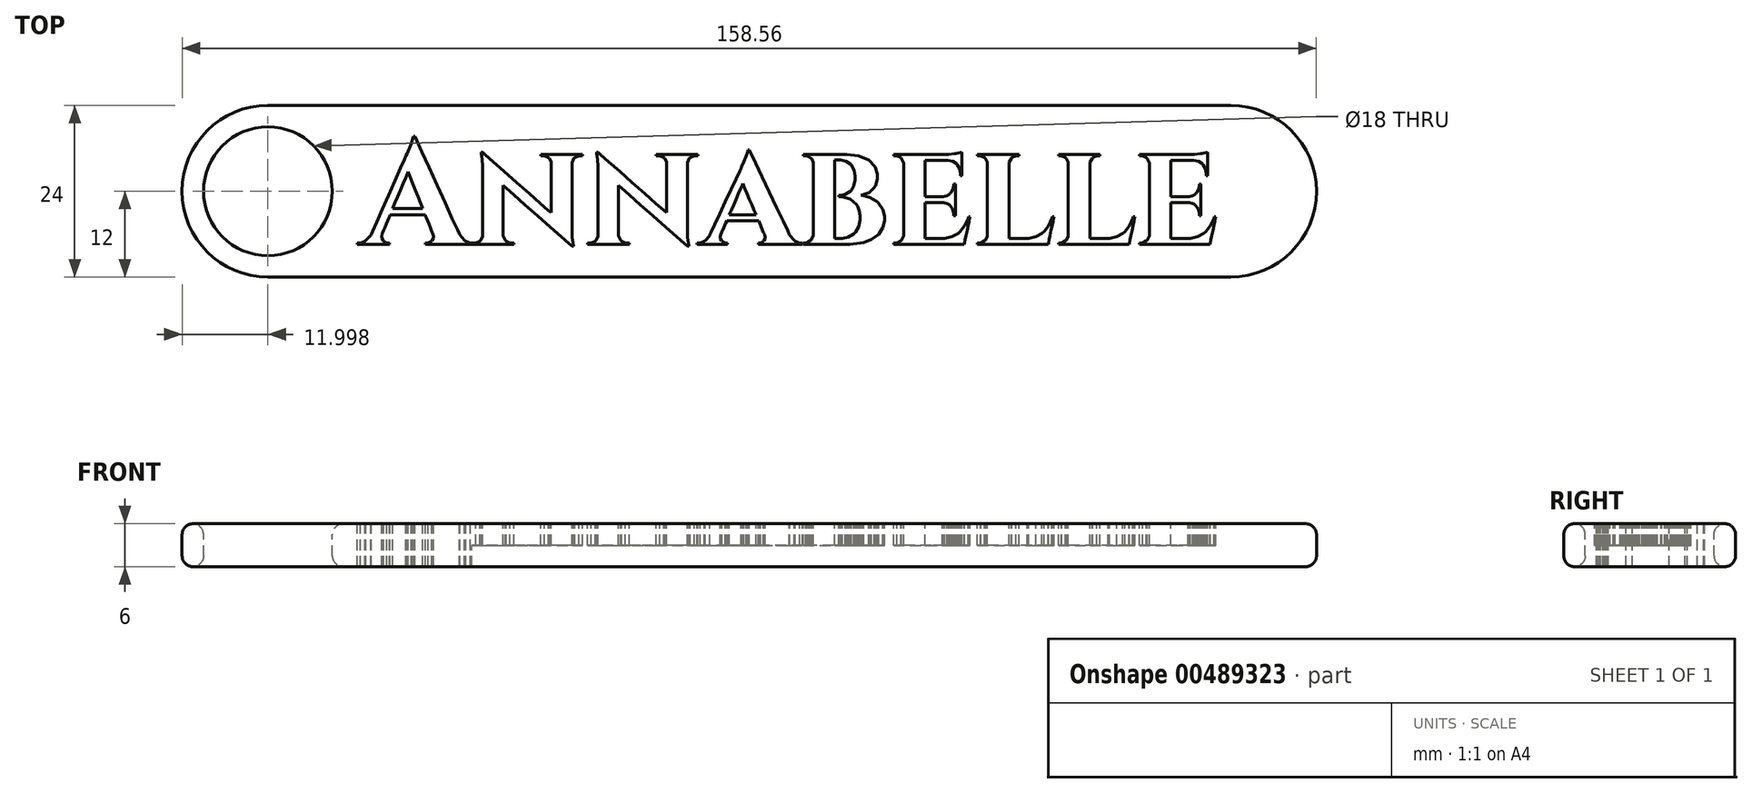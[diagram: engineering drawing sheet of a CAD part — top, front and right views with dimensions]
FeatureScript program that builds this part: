
annotation { "Feature Type Name" : "Feature", "Feature Type Description" : "" }
export const myFeature = defineFeature(function(context is Context, id is Id, definition is map)
    precondition{}
    {
        {
            var Q0;
            Q0=qCreatedBy(makeId("Top.planeOp"),FACE);
            var sketch = newSketch(context, id + "F0", { "sketchPlane" : qUnion([Q0])});
            skLineSegment(sketch, "E0", {"start": v(-43.95, -7.2) * mm, "end": v(-43.76, -7.2) * mm});
            skLineSegment(sketch, "E1", {"start": v(-43.76, -7.2) * mm, "end": v(-43.76, -7.31) * mm});
            skLineSegment(sketch, "E2", {"start": v(-43.76, -7.31) * mm, "end": v(-43.76, -7.42) * mm});
            skLineSegment(sketch, "E3", {"start": v(-43.76, -7.42) * mm, "end": v(-44.05, -7.42) * mm});
            skLineSegment(sketch, "E4", {"start": v(-44.05, -7.42) * mm, "end": v(-44.8, -7.42) * mm});
            skLineSegment(sketch, "E5", {"start": v(-44.8, -7.42) * mm, "end": v(-45.88, -7.42) * mm});
            skLineSegment(sketch, "E6", {"start": v(-45.88, -7.42) * mm, "end": v(-47.1, -7.42) * mm});
            skLineSegment(sketch, "E7", {"start": v(-47.1, -7.42) * mm, "end": v(-48.34, -7.42) * mm});
            skLineSegment(sketch, "E8", {"start": v(-48.34, -7.42) * mm, "end": v(-49.4, -7.42) * mm});
            skLineSegment(sketch, "E9", {"start": v(-49.4, -7.42) * mm, "end": v(-50.17, -7.42) * mm});
            skLineSegment(sketch, "E10", {"start": v(-50.17, -7.42) * mm, "end": v(-50.45, -7.42) * mm});
            skLineSegment(sketch, "E11", {"start": v(-50.45, -7.42) * mm, "end": v(-50.45, -7.31) * mm});
            skLineSegment(sketch, "E12", {"start": v(-50.45, -7.31) * mm, "end": v(-50.45, -7.2) * mm});
            skLineSegment(sketch, "E13", {"start": v(-50.45, -7.2) * mm, "end": v(-50.26, -7.2) * mm});
            skLineSegment(sketch, "E14", {"start": v(-50.26, -7.2) * mm, "end": v(-50.1, -7.2) * mm});
            skLineSegment(sketch, "E15", {"start": v(-50.1, -7.2) * mm, "end": v(-49.62, -6.97) * mm});
            skLineSegment(sketch, "E16", {"start": v(-49.62, -6.97) * mm, "end": v(-49.58, -6.92) * mm});
            skLineSegment(sketch, "E17", {"start": v(-49.58, -6.92) * mm, "end": v(-49.55, -6.88) * mm});
            skLineSegment(sketch, "E18", {"start": v(-49.55, -6.88) * mm, "end": v(-49.36, -6.51) * mm});
            skLineSegment(sketch, "E19", {"start": v(-49.36, -6.51) * mm, "end": v(-49.36, -6.39) * mm});
            skLineSegment(sketch, "E20", {"start": v(-49.36, -6.39) * mm, "end": v(-49.36, -6.26) * mm});
            skLineSegment(sketch, "E21", {"start": v(-49.36, -6.26) * mm, "end": v(-49.45, -5.93) * mm});
            skLineSegment(sketch, "E22", {"start": v(-49.45, -5.93) * mm, "end": v(-49.47, -5.89) * mm});
            skLineSegment(sketch, "E23", {"start": v(-49.47, -5.89) * mm, "end": v(-49.51, -5.77) * mm});
            skLineSegment(sketch, "E24", {"start": v(-49.51, -5.77) * mm, "end": v(-49.63, -5.48) * mm});
            skLineSegment(sketch, "E25", {"start": v(-49.63, -5.48) * mm, "end": v(-49.8, -5.07) * mm});
            skLineSegment(sketch, "E26", {"start": v(-49.8, -5.07) * mm, "end": v(-49.98, -4.6) * mm});
            skLineSegment(sketch, "E27", {"start": v(-49.98, -4.6) * mm, "end": v(-50.17, -4.12) * mm});
            skLineSegment(sketch, "E28", {"start": v(-50.17, -4.12) * mm, "end": v(-50.33, -3.7) * mm});
            skLineSegment(sketch, "E29", {"start": v(-50.33, -3.7) * mm, "end": v(-50.45, -3.42) * mm});
            skLineSegment(sketch, "E30", {"start": v(-50.45, -3.42) * mm, "end": v(-50.5, -3.3) * mm});
            skLineSegment(sketch, "E31", {"start": v(-50.5, -3.3) * mm, "end": v(-50.7, -3.3) * mm});
            skLineSegment(sketch, "E32", {"start": v(-50.7, -3.3) * mm, "end": v(-51.26, -3.3) * mm});
            skLineSegment(sketch, "E33", {"start": v(-51.26, -3.3) * mm, "end": v(-52.05, -3.3) * mm});
            skLineSegment(sketch, "E34", {"start": v(-52.05, -3.3) * mm, "end": v(-52.95, -3.3) * mm});
            skLineSegment(sketch, "E35", {"start": v(-52.95, -3.3) * mm, "end": v(-53.85, -3.3) * mm});
            skLineSegment(sketch, "E36", {"start": v(-53.85, -3.3) * mm, "end": v(-54.64, -3.3) * mm});
            skLineSegment(sketch, "E37", {"start": v(-54.64, -3.3) * mm, "end": v(-55.2, -3.3) * mm});
            skLineSegment(sketch, "E38", {"start": v(-55.2, -3.3) * mm, "end": v(-55.4, -3.3) * mm});
            skLineSegment(sketch, "E39", {"start": v(-55.4, -3.3) * mm, "end": v(-55.45, -3.42) * mm});
            skLineSegment(sketch, "E40", {"start": v(-55.45, -3.42) * mm, "end": v(-55.58, -3.7) * mm});
            skLineSegment(sketch, "E41", {"start": v(-55.58, -3.7) * mm, "end": v(-55.75, -4.12) * mm});
            skLineSegment(sketch, "E42", {"start": v(-55.75, -4.12) * mm, "end": v(-55.95, -4.6) * mm});
            skLineSegment(sketch, "E43", {"start": v(-55.95, -4.6) * mm, "end": v(-56.15, -5.07) * mm});
            skLineSegment(sketch, "E44", {"start": v(-56.15, -5.07) * mm, "end": v(-56.33, -5.48) * mm});
            skLineSegment(sketch, "E45", {"start": v(-56.33, -5.48) * mm, "end": v(-56.45, -5.77) * mm});
            skLineSegment(sketch, "E46", {"start": v(-56.45, -5.77) * mm, "end": v(-56.5, -5.89) * mm});
            skLineSegment(sketch, "E47", {"start": v(-56.5, -5.89) * mm, "end": v(-56.51, -5.93) * mm});
            skLineSegment(sketch, "E48", {"start": v(-56.51, -5.93) * mm, "end": v(-56.6, -6.28) * mm});
            skLineSegment(sketch, "E49", {"start": v(-56.6, -6.28) * mm, "end": v(-56.6, -6.4) * mm});
            skLineSegment(sketch, "E50", {"start": v(-56.6, -6.4) * mm, "end": v(-56.6, -6.53) * mm});
            skLineSegment(sketch, "E51", {"start": v(-56.6, -6.53) * mm, "end": v(-56.4, -6.88) * mm});
            skLineSegment(sketch, "E52", {"start": v(-56.4, -6.88) * mm, "end": v(-56.37, -6.92) * mm});
            skLineSegment(sketch, "E53", {"start": v(-56.37, -6.92) * mm, "end": v(-56.33, -6.97) * mm});
            skLineSegment(sketch, "E54", {"start": v(-56.33, -6.97) * mm, "end": v(-55.84, -7.2) * mm});
            skLineSegment(sketch, "E55", {"start": v(-55.84, -7.2) * mm, "end": v(-55.68, -7.2) * mm});
            skLineSegment(sketch, "E56", {"start": v(-55.68, -7.2) * mm, "end": v(-55.51, -7.2) * mm});
            skLineSegment(sketch, "E57", {"start": v(-55.51, -7.2) * mm, "end": v(-55.51, -7.31) * mm});
            skLineSegment(sketch, "E58", {"start": v(-55.51, -7.31) * mm, "end": v(-55.51, -7.42) * mm});
            skLineSegment(sketch, "E59", {"start": v(-55.51, -7.42) * mm, "end": v(-55.7, -7.42) * mm});
            skLineSegment(sketch, "E60", {"start": v(-55.7, -7.42) * mm, "end": v(-56.21, -7.42) * mm});
            skLineSegment(sketch, "E61", {"start": v(-56.21, -7.42) * mm, "end": v(-56.93, -7.42) * mm});
            skLineSegment(sketch, "E62", {"start": v(-56.93, -7.42) * mm, "end": v(-57.76, -7.42) * mm});
            skLineSegment(sketch, "E63", {"start": v(-57.76, -7.42) * mm, "end": v(-58.58, -7.42) * mm});
            skLineSegment(sketch, "E64", {"start": v(-58.58, -7.42) * mm, "end": v(-59.3, -7.42) * mm});
            skLineSegment(sketch, "E65", {"start": v(-59.3, -7.42) * mm, "end": v(-59.8, -7.42) * mm});
            skLineSegment(sketch, "E66", {"start": v(-59.8, -7.42) * mm, "end": v(-60, -7.42) * mm});
            skLineSegment(sketch, "E67", {"start": v(-60, -7.42) * mm, "end": v(-60, -7.31) * mm});
            skLineSegment(sketch, "E68", {"start": v(-60, -7.31) * mm, "end": v(-60, -7.2) * mm});
            skLineSegment(sketch, "E69", {"start": v(-60, -7.2) * mm, "end": v(-59.81, -7.2) * mm});
            skLineSegment(sketch, "E70", {"start": v(-59.81, -7.2) * mm, "end": v(-59.57, -7.2) * mm});
            skLineSegment(sketch, "E71", {"start": v(-59.57, -7.2) * mm, "end": v(-58.93, -6.96) * mm});
            skLineSegment(sketch, "E72", {"start": v(-58.93, -6.96) * mm, "end": v(-58.85, -6.91) * mm});
            skLineSegment(sketch, "E73", {"start": v(-58.85, -6.91) * mm, "end": v(-58.77, -6.86) * mm});
            skLineSegment(sketch, "E74", {"start": v(-58.77, -6.86) * mm, "end": v(-58.1, -6.13) * mm});
            skLineSegment(sketch, "E75", {"start": v(-58.1, -6.13) * mm, "end": v(-58.05, -6.03) * mm});
            skLineSegment(sketch, "E76", {"start": v(-58.05, -6.03) * mm, "end": v(-57.84, -5.56) * mm});
            skLineSegment(sketch, "E77", {"start": v(-57.84, -5.56) * mm, "end": v(-57.3, -4.32) * mm});
            skLineSegment(sketch, "E78", {"start": v(-57.3, -4.32) * mm, "end": v(-56.52, -2.56) * mm});
            skLineSegment(sketch, "E79", {"start": v(-56.52, -2.56) * mm, "end": v(-55.63, -0.55) * mm});
            skLineSegment(sketch, "E80", {"start": v(-55.63, -0.55) * mm, "end": v(-54.74, 1.47) * mm});
            skLineSegment(sketch, "E81", {"start": v(-54.74, 1.47) * mm, "end": v(-53.96, 3.23) * mm});
            skLineSegment(sketch, "E82", {"start": v(-53.96, 3.23) * mm, "end": v(-53.41, 4.47) * mm});
            skLineSegment(sketch, "E83", {"start": v(-53.41, 4.47) * mm, "end": v(-53.2, 4.94) * mm});
            skLineSegment(sketch, "E84", {"start": v(-53.2, 4.94) * mm, "end": v(-53.04, 5.29) * mm});
            skLineSegment(sketch, "E85", {"start": v(-53.04, 5.29) * mm, "end": v(-52.45, 6.67) * mm});
            skLineSegment(sketch, "E86", {"start": v(-52.45, 6.67) * mm, "end": v(-52.16, 7.58) * mm});
            skLineSegment(sketch, "E87", {"start": v(-52.16, 7.58) * mm, "end": v(-52.15, 7.7) * mm});
            skLineSegment(sketch, "E88", {"start": v(-52.15, 7.7) * mm, "end": v(-51.96, 7.7) * mm});
            skLineSegment(sketch, "E89", {"start": v(-51.96, 7.7) * mm, "end": v(-51.7, 7.1) * mm});
            skLineSegment(sketch, "E90", {"start": v(-51.7, 7.1) * mm, "end": v(-51, 5.55) * mm});
            skLineSegment(sketch, "E91", {"start": v(-51, 5.55) * mm, "end": v(-50, 3.36) * mm});
            skLineSegment(sketch, "E92", {"start": v(-50, 3.36) * mm, "end": v(-48.85, 0.85) * mm});
            skLineSegment(sketch, "E93", {"start": v(-48.85, 0.85) * mm, "end": v(-47.7, -1.66) * mm});
            skLineSegment(sketch, "E94", {"start": v(-47.7, -1.66) * mm, "end": v(-46.7, -3.85) * mm});
            skLineSegment(sketch, "E95", {"start": v(-46.7, -3.85) * mm, "end": v(-46, -5.4) * mm});
            skLineSegment(sketch, "E96", {"start": v(-46, -5.4) * mm, "end": v(-45.73, -6) * mm});
            skLineSegment(sketch, "E97", {"start": v(-45.73, -6) * mm, "end": v(-45.68, -6.1) * mm});
            skLineSegment(sketch, "E98", {"start": v(-45.68, -6.1) * mm, "end": v(-45.02, -6.85) * mm});
            skLineSegment(sketch, "E99", {"start": v(-45.02, -6.85) * mm, "end": v(-44.94, -6.9) * mm});
            skLineSegment(sketch, "E100", {"start": v(-44.94, -6.9) * mm, "end": v(-44.86, -6.95) * mm});
            skLineSegment(sketch, "E101", {"start": v(-44.86, -6.95) * mm, "end": v(-44.18, -7.2) * mm});
            skLineSegment(sketch, "E102", {"start": v(-44.18, -7.2) * mm, "end": v(-43.95, -7.2) * mm});
            skLineSegment(sketch, "E103", {"start": v(-55.05, -2.42) * mm, "end": v(-54.87, -2.42) * mm});
            skLineSegment(sketch, "E104", {"start": v(-54.87, -2.42) * mm, "end": v(-54.4, -2.42) * mm});
            skLineSegment(sketch, "E105", {"start": v(-54.4, -2.42) * mm, "end": v(-53.72, -2.42) * mm});
            skLineSegment(sketch, "E106", {"start": v(-53.72, -2.42) * mm, "end": v(-52.95, -2.42) * mm});
            skLineSegment(sketch, "E107", {"start": v(-52.95, -2.42) * mm, "end": v(-52.18, -2.42) * mm});
            skLineSegment(sketch, "E108", {"start": v(-52.18, -2.42) * mm, "end": v(-51.5, -2.42) * mm});
            skLineSegment(sketch, "E109", {"start": v(-51.5, -2.42) * mm, "end": v(-51.03, -2.42) * mm});
            skLineSegment(sketch, "E110", {"start": v(-51.03, -2.42) * mm, "end": v(-50.85, -2.42) * mm});
            skLineSegment(sketch, "E111", {"start": v(-50.85, -2.42) * mm, "end": v(-50.94, -2.2) * mm});
            skLineSegment(sketch, "E112", {"start": v(-50.94, -2.2) * mm, "end": v(-51.17, -1.62) * mm});
            skLineSegment(sketch, "E113", {"start": v(-51.17, -1.62) * mm, "end": v(-51.5, -0.79) * mm});
            skLineSegment(sketch, "E114", {"start": v(-51.5, -0.79) * mm, "end": v(-51.87, 0.16) * mm});
            skLineSegment(sketch, "E115", {"start": v(-51.87, 0.16) * mm, "end": v(-52.24, 1.1) * mm});
            skLineSegment(sketch, "E116", {"start": v(-52.24, 1.1) * mm, "end": v(-52.57, 1.93) * mm});
            skLineSegment(sketch, "E117", {"start": v(-52.57, 1.93) * mm, "end": v(-52.8, 2.52) * mm});
            skLineSegment(sketch, "E118", {"start": v(-52.8, 2.52) * mm, "end": v(-52.89, 2.74) * mm});
            skLineSegment(sketch, "E119", {"start": v(-52.89, 2.74) * mm, "end": v(-52.98, 2.52) * mm});
            skLineSegment(sketch, "E120", {"start": v(-52.98, 2.52) * mm, "end": v(-53.23, 1.93) * mm});
            skLineSegment(sketch, "E121", {"start": v(-53.23, 1.93) * mm, "end": v(-53.57, 1.1) * mm});
            skLineSegment(sketch, "E122", {"start": v(-53.57, 1.1) * mm, "end": v(-53.97, 0.16) * mm});
            skLineSegment(sketch, "E123", {"start": v(-53.97, 0.16) * mm, "end": v(-54.37, -0.79) * mm});
            skLineSegment(sketch, "E124", {"start": v(-54.37, -0.79) * mm, "end": v(-54.71, -1.62) * mm});
            skLineSegment(sketch, "E125", {"start": v(-54.71, -1.62) * mm, "end": v(-54.96, -2.2) * mm});
            skLineSegment(sketch, "E126", {"start": v(-54.96, -2.2) * mm, "end": v(-55.05, -2.42) * mm});
            skLineSegment(sketch, "E127", {"start": v(-34.38, 5.17) * mm, "end": v(-33.46, 5.17) * mm});
            skLineSegment(sketch, "E128", {"start": v(-33.46, 5.17) * mm, "end": v(-31.43, 5.17) * mm});
            skLineSegment(sketch, "E129", {"start": v(-31.43, 5.17) * mm, "end": v(-29.4, 5.17) * mm});
            skLineSegment(sketch, "E130", {"start": v(-29.4, 5.17) * mm, "end": v(-28.48, 5.17) * mm});
            skLineSegment(sketch, "E131", {"start": v(-28.48, 5.17) * mm, "end": v(-28.48, 5.07) * mm});
            skLineSegment(sketch, "E132", {"start": v(-28.48, 5.07) * mm, "end": v(-28.48, 4.96) * mm});
            skLineSegment(sketch, "E133", {"start": v(-28.48, 4.96) * mm, "end": v(-28.66, 4.96) * mm});
            skLineSegment(sketch, "E134", {"start": v(-28.66, 4.96) * mm, "end": v(-28.84, 4.96) * mm});
            skLineSegment(sketch, "E135", {"start": v(-28.84, 4.96) * mm, "end": v(-29.04, 4.96) * mm});
            skLineSegment(sketch, "E136", {"start": v(-29.04, 4.96) * mm, "end": v(-29.6, 4.72) * mm});
            skLineSegment(sketch, "E137", {"start": v(-29.6, 4.72) * mm, "end": v(-29.65, 4.67) * mm});
            skLineSegment(sketch, "E138", {"start": v(-29.65, 4.67) * mm, "end": v(-29.7, 4.62) * mm});
            skLineSegment(sketch, "E139", {"start": v(-29.7, 4.62) * mm, "end": v(-30, 4) * mm});
            skLineSegment(sketch, "E140", {"start": v(-30, 4) * mm, "end": v(-30, 3.91) * mm});
            skLineSegment(sketch, "E141", {"start": v(-30, 3.91) * mm, "end": v(-30, 3.52) * mm});
            skLineSegment(sketch, "E142", {"start": v(-30, 3.52) * mm, "end": v(-30, 2.48) * mm});
            skLineSegment(sketch, "E143", {"start": v(-30, 2.48) * mm, "end": v(-30, 1.01) * mm});
            skLineSegment(sketch, "E144", {"start": v(-30, 1.01) * mm, "end": v(-30, -0.67) * mm});
            skLineSegment(sketch, "E145", {"start": v(-30, -0.67) * mm, "end": v(-30, -2.35) * mm});
            skLineSegment(sketch, "E146", {"start": v(-30, -2.35) * mm, "end": v(-30, -3.82) * mm});
            skLineSegment(sketch, "E147", {"start": v(-30, -3.82) * mm, "end": v(-30, -4.86) * mm});
            skLineSegment(sketch, "E148", {"start": v(-30, -4.86) * mm, "end": v(-30, -5.26) * mm});
            skLineSegment(sketch, "E149", {"start": v(-30, -5.26) * mm, "end": v(-30, -5.55) * mm});
            skLineSegment(sketch, "E150", {"start": v(-30, -5.55) * mm, "end": v(-29.95, -6.44) * mm});
            skLineSegment(sketch, "E151", {"start": v(-29.95, -6.44) * mm, "end": v(-29.86, -7.26) * mm});
            skLineSegment(sketch, "E152", {"start": v(-29.86, -7.26) * mm, "end": v(-29.83, -7.4) * mm});
            skLineSegment(sketch, "E153", {"start": v(-29.83, -7.4) * mm, "end": v(-29.8, -7.54) * mm});
            skLineSegment(sketch, "E154", {"start": v(-29.8, -7.54) * mm, "end": v(-29.78, -7.7) * mm});
            skLineSegment(sketch, "E155", {"start": v(-29.78, -7.7) * mm, "end": v(-29.97, -7.7) * mm});
            skLineSegment(sketch, "E156", {"start": v(-29.97, -7.7) * mm, "end": v(-30.39, -7.32) * mm});
            skLineSegment(sketch, "E157", {"start": v(-30.39, -7.32) * mm, "end": v(-31.48, -6.36) * mm});
            skLineSegment(sketch, "E158", {"start": v(-31.48, -6.36) * mm, "end": v(-33.02, -5) * mm});
            skLineSegment(sketch, "E159", {"start": v(-33.02, -5) * mm, "end": v(-34.8, -3.44) * mm});
            skLineSegment(sketch, "E160", {"start": v(-34.8, -3.44) * mm, "end": v(-36.56, -1.88) * mm});
            skLineSegment(sketch, "E161", {"start": v(-36.56, -1.88) * mm, "end": v(-38.1, -0.52) * mm});
            skLineSegment(sketch, "E162", {"start": v(-38.1, -0.52) * mm, "end": v(-39.2, 0.44) * mm});
            skLineSegment(sketch, "E163", {"start": v(-39.2, 0.44) * mm, "end": v(-39.6, 0.8) * mm});
            skLineSegment(sketch, "E164", {"start": v(-39.6, 0.8) * mm, "end": v(-39.6, 0.51) * mm});
            skLineSegment(sketch, "E165", {"start": v(-39.6, 0.51) * mm, "end": v(-39.6, -0.28) * mm});
            skLineSegment(sketch, "E166", {"start": v(-39.6, -0.28) * mm, "end": v(-39.6, -1.39) * mm});
            skLineSegment(sketch, "E167", {"start": v(-39.6, -1.39) * mm, "end": v(-39.6, -2.66) * mm});
            skLineSegment(sketch, "E168", {"start": v(-39.6, -2.66) * mm, "end": v(-39.6, -3.94) * mm});
            skLineSegment(sketch, "E169", {"start": v(-39.6, -3.94) * mm, "end": v(-39.6, -5.05) * mm});
            skLineSegment(sketch, "E170", {"start": v(-39.6, -5.05) * mm, "end": v(-39.6, -5.84) * mm});
            skLineSegment(sketch, "E171", {"start": v(-39.6, -5.84) * mm, "end": v(-39.6, -6.14) * mm});
            skLineSegment(sketch, "E172", {"start": v(-39.6, -6.14) * mm, "end": v(-39.6, -6.21) * mm});
            skLineSegment(sketch, "E173", {"start": v(-39.6, -6.21) * mm, "end": v(-39.31, -6.85) * mm});
            skLineSegment(sketch, "E174", {"start": v(-39.31, -6.85) * mm, "end": v(-39.26, -6.9) * mm});
            skLineSegment(sketch, "E175", {"start": v(-39.26, -6.9) * mm, "end": v(-39.2, -6.95) * mm});
            skLineSegment(sketch, "E176", {"start": v(-39.2, -6.95) * mm, "end": v(-38.64, -7.2) * mm});
            skLineSegment(sketch, "E177", {"start": v(-38.64, -7.2) * mm, "end": v(-38.45, -7.2) * mm});
            skLineSegment(sketch, "E178", {"start": v(-38.45, -7.2) * mm, "end": v(-38.27, -7.2) * mm});
            skLineSegment(sketch, "E179", {"start": v(-38.27, -7.2) * mm, "end": v(-38.1, -7.2) * mm});
            skLineSegment(sketch, "E180", {"start": v(-38.1, -7.2) * mm, "end": v(-38.1, -7.31) * mm});
            skLineSegment(sketch, "E181", {"start": v(-38.1, -7.31) * mm, "end": v(-38.1, -7.42) * mm});
            skLineSegment(sketch, "E182", {"start": v(-38.1, -7.42) * mm, "end": v(-39.01, -7.42) * mm});
            skLineSegment(sketch, "E183", {"start": v(-39.01, -7.42) * mm, "end": v(-41.03, -7.42) * mm});
            skLineSegment(sketch, "E184", {"start": v(-41.03, -7.42) * mm, "end": v(-43.05, -7.42) * mm});
            skLineSegment(sketch, "E185", {"start": v(-43.05, -7.42) * mm, "end": v(-43.97, -7.42) * mm});
            skLineSegment(sketch, "E186", {"start": v(-43.97, -7.42) * mm, "end": v(-43.97, -7.31) * mm});
            skLineSegment(sketch, "E187", {"start": v(-43.97, -7.31) * mm, "end": v(-43.97, -7.2) * mm});
            skLineSegment(sketch, "E188", {"start": v(-43.97, -7.2) * mm, "end": v(-43.8, -7.2) * mm});
            skLineSegment(sketch, "E189", {"start": v(-43.8, -7.2) * mm, "end": v(-43.63, -7.2) * mm});
            skLineSegment(sketch, "E190", {"start": v(-43.63, -7.2) * mm, "end": v(-43.43, -7.2) * mm});
            skLineSegment(sketch, "E191", {"start": v(-43.43, -7.2) * mm, "end": v(-42.87, -6.95) * mm});
            skLineSegment(sketch, "E192", {"start": v(-42.87, -6.95) * mm, "end": v(-42.82, -6.9) * mm});
            skLineSegment(sketch, "E193", {"start": v(-42.82, -6.9) * mm, "end": v(-42.76, -6.85) * mm});
            skLineSegment(sketch, "E194", {"start": v(-42.76, -6.85) * mm, "end": v(-42.48, -6.32) * mm});
            skLineSegment(sketch, "E195", {"start": v(-42.48, -6.32) * mm, "end": v(-42.48, -6.14) * mm});
            skLineSegment(sketch, "E196", {"start": v(-42.48, -6.14) * mm, "end": v(-42.48, -5.74) * mm});
            skLineSegment(sketch, "E197", {"start": v(-42.48, -5.74) * mm, "end": v(-42.48, -4.7) * mm});
            skLineSegment(sketch, "E198", {"start": v(-42.48, -4.7) * mm, "end": v(-42.48, -3.22) * mm});
            skLineSegment(sketch, "E199", {"start": v(-42.48, -3.22) * mm, "end": v(-42.48, -1.52) * mm});
            skLineSegment(sketch, "E200", {"start": v(-42.48, -1.52) * mm, "end": v(-42.48, 0.17) * mm});
            skLineSegment(sketch, "E201", {"start": v(-42.48, 0.17) * mm, "end": v(-42.48, 1.65) * mm});
            skLineSegment(sketch, "E202", {"start": v(-42.48, 1.65) * mm, "end": v(-42.48, 2.7) * mm});
            skLineSegment(sketch, "E203", {"start": v(-42.48, 2.7) * mm, "end": v(-42.48, 3.1) * mm});
            skLineSegment(sketch, "E204", {"start": v(-42.48, 3.1) * mm, "end": v(-42.48, 3.61) * mm});
            skLineSegment(sketch, "E205", {"start": v(-42.48, 3.61) * mm, "end": v(-42.62, 5.04) * mm});
            skLineSegment(sketch, "E206", {"start": v(-42.62, 5.04) * mm, "end": v(-42.65, 5.17) * mm});
            skLineSegment(sketch, "E207", {"start": v(-42.65, 5.17) * mm, "end": v(-42.67, 5.32) * mm});
            skLineSegment(sketch, "E208", {"start": v(-42.67, 5.32) * mm, "end": v(-42.69, 5.47) * mm});
            skLineSegment(sketch, "E209", {"start": v(-42.69, 5.47) * mm, "end": v(-42.6, 5.46) * mm});
            skLineSegment(sketch, "E210", {"start": v(-42.6, 5.46) * mm, "end": v(-42.5, 5.45) * mm});
            skLineSegment(sketch, "E211", {"start": v(-42.5, 5.45) * mm, "end": v(-42.09, 5.08) * mm});
            skLineSegment(sketch, "E212", {"start": v(-42.09, 5.08) * mm, "end": v(-41, 4.13) * mm});
            skLineSegment(sketch, "E213", {"start": v(-41, 4.13) * mm, "end": v(-39.46, 2.77) * mm});
            skLineSegment(sketch, "E214", {"start": v(-39.46, 2.77) * mm, "end": v(-37.7, 1.22) * mm});
            skLineSegment(sketch, "E215", {"start": v(-37.7, 1.22) * mm, "end": v(-35.93, -0.34) * mm});
            skLineSegment(sketch, "E216", {"start": v(-35.93, -0.34) * mm, "end": v(-34.4, -1.69) * mm});
            skLineSegment(sketch, "E217", {"start": v(-34.4, -1.69) * mm, "end": v(-33.3, -2.65) * mm});
            skLineSegment(sketch, "E218", {"start": v(-33.3, -2.65) * mm, "end": v(-32.9, -3.01) * mm});
            skLineSegment(sketch, "E219", {"start": v(-32.9, -3.01) * mm, "end": v(-32.9, -2.71) * mm});
            skLineSegment(sketch, "E220", {"start": v(-32.9, -2.71) * mm, "end": v(-32.9, -1.93) * mm});
            skLineSegment(sketch, "E221", {"start": v(-32.9, -1.93) * mm, "end": v(-32.9, -0.83) * mm});
            skLineSegment(sketch, "E222", {"start": v(-32.9, -0.83) * mm, "end": v(-32.9, 0.44) * mm});
            skLineSegment(sketch, "E223", {"start": v(-32.9, 0.44) * mm, "end": v(-32.9, 1.7) * mm});
            skLineSegment(sketch, "E224", {"start": v(-32.9, 1.7) * mm, "end": v(-32.9, 2.81) * mm});
            skLineSegment(sketch, "E225", {"start": v(-32.9, 2.81) * mm, "end": v(-32.9, 3.6) * mm});
            skLineSegment(sketch, "E226", {"start": v(-32.9, 3.6) * mm, "end": v(-32.9, 3.9) * mm});
            skLineSegment(sketch, "E227", {"start": v(-32.9, 3.9) * mm, "end": v(-32.9, 4.08) * mm});
            skLineSegment(sketch, "E228", {"start": v(-32.9, 4.08) * mm, "end": v(-33.16, 4.6) * mm});
            skLineSegment(sketch, "E229", {"start": v(-33.16, 4.6) * mm, "end": v(-33.22, 4.66) * mm});
            skLineSegment(sketch, "E230", {"start": v(-33.22, 4.66) * mm, "end": v(-33.27, 4.7) * mm});
            skLineSegment(sketch, "E231", {"start": v(-33.27, 4.7) * mm, "end": v(-33.84, 4.96) * mm});
            skLineSegment(sketch, "E232", {"start": v(-33.84, 4.96) * mm, "end": v(-34.02, 4.96) * mm});
            skLineSegment(sketch, "E233", {"start": v(-34.02, 4.96) * mm, "end": v(-34.2, 4.96) * mm});
            skLineSegment(sketch, "E234", {"start": v(-34.2, 4.96) * mm, "end": v(-34.38, 4.96) * mm});
            skLineSegment(sketch, "E235", {"start": v(-34.38, 4.96) * mm, "end": v(-34.38, 5.07) * mm});
            skLineSegment(sketch, "E236", {"start": v(-34.38, 5.07) * mm, "end": v(-34.38, 5.17) * mm});
            skLineSegment(sketch, "E237", {"start": v(-18.24, 5.17) * mm, "end": v(-17.32, 5.17) * mm});
            skLineSegment(sketch, "E238", {"start": v(-17.32, 5.17) * mm, "end": v(-15.3, 5.17) * mm});
            skLineSegment(sketch, "E239", {"start": v(-15.3, 5.17) * mm, "end": v(-13.27, 5.17) * mm});
            skLineSegment(sketch, "E240", {"start": v(-13.27, 5.17) * mm, "end": v(-12.35, 5.17) * mm});
            skLineSegment(sketch, "E241", {"start": v(-12.35, 5.17) * mm, "end": v(-12.35, 5.07) * mm});
            skLineSegment(sketch, "E242", {"start": v(-12.35, 5.07) * mm, "end": v(-12.35, 4.96) * mm});
            skLineSegment(sketch, "E243", {"start": v(-12.35, 4.96) * mm, "end": v(-12.53, 4.96) * mm});
            skLineSegment(sketch, "E244", {"start": v(-12.53, 4.96) * mm, "end": v(-12.7, 4.96) * mm});
            skLineSegment(sketch, "E245", {"start": v(-12.7, 4.96) * mm, "end": v(-12.9, 4.96) * mm});
            skLineSegment(sketch, "E246", {"start": v(-12.9, 4.96) * mm, "end": v(-13.46, 4.72) * mm});
            skLineSegment(sketch, "E247", {"start": v(-13.46, 4.72) * mm, "end": v(-13.51, 4.67) * mm});
            skLineSegment(sketch, "E248", {"start": v(-13.51, 4.67) * mm, "end": v(-13.57, 4.62) * mm});
            skLineSegment(sketch, "E249", {"start": v(-13.57, 4.62) * mm, "end": v(-13.86, 4) * mm});
            skLineSegment(sketch, "E250", {"start": v(-13.86, 4) * mm, "end": v(-13.86, 3.91) * mm});
            skLineSegment(sketch, "E251", {"start": v(-13.86, 3.91) * mm, "end": v(-13.86, 3.52) * mm});
            skLineSegment(sketch, "E252", {"start": v(-13.86, 3.52) * mm, "end": v(-13.86, 2.48) * mm});
            skLineSegment(sketch, "E253", {"start": v(-13.86, 2.48) * mm, "end": v(-13.86, 1.01) * mm});
            skLineSegment(sketch, "E254", {"start": v(-13.86, 1.01) * mm, "end": v(-13.86, -0.67) * mm});
            skLineSegment(sketch, "E255", {"start": v(-13.86, -0.67) * mm, "end": v(-13.86, -2.35) * mm});
            skLineSegment(sketch, "E256", {"start": v(-13.86, -2.35) * mm, "end": v(-13.86, -3.82) * mm});
            skLineSegment(sketch, "E257", {"start": v(-13.86, -3.82) * mm, "end": v(-13.86, -4.86) * mm});
            skLineSegment(sketch, "E258", {"start": v(-13.86, -4.86) * mm, "end": v(-13.86, -5.26) * mm});
            skLineSegment(sketch, "E259", {"start": v(-13.86, -5.26) * mm, "end": v(-13.86, -5.55) * mm});
            skLineSegment(sketch, "E260", {"start": v(-13.86, -5.55) * mm, "end": v(-13.82, -6.44) * mm});
            skLineSegment(sketch, "E261", {"start": v(-13.82, -6.44) * mm, "end": v(-13.72, -7.26) * mm});
            skLineSegment(sketch, "E262", {"start": v(-13.72, -7.26) * mm, "end": v(-13.7, -7.4) * mm});
            skLineSegment(sketch, "E263", {"start": v(-13.7, -7.4) * mm, "end": v(-13.67, -7.54) * mm});
            skLineSegment(sketch, "E264", {"start": v(-13.67, -7.54) * mm, "end": v(-13.65, -7.7) * mm});
            skLineSegment(sketch, "E265", {"start": v(-13.65, -7.7) * mm, "end": v(-13.84, -7.7) * mm});
            skLineSegment(sketch, "E266", {"start": v(-13.84, -7.7) * mm, "end": v(-14.25, -7.32) * mm});
            skLineSegment(sketch, "E267", {"start": v(-14.25, -7.32) * mm, "end": v(-15.34, -6.36) * mm});
            skLineSegment(sketch, "E268", {"start": v(-15.34, -6.36) * mm, "end": v(-16.89, -5) * mm});
            skLineSegment(sketch, "E269", {"start": v(-16.89, -5) * mm, "end": v(-18.65, -3.44) * mm});
            skLineSegment(sketch, "E270", {"start": v(-18.65, -3.44) * mm, "end": v(-20.42, -1.88) * mm});
            skLineSegment(sketch, "E271", {"start": v(-20.42, -1.88) * mm, "end": v(-21.97, -0.52) * mm});
            skLineSegment(sketch, "E272", {"start": v(-21.97, -0.52) * mm, "end": v(-23.06, 0.44) * mm});
            skLineSegment(sketch, "E273", {"start": v(-23.06, 0.44) * mm, "end": v(-23.47, 0.8) * mm});
            skLineSegment(sketch, "E274", {"start": v(-23.47, 0.8) * mm, "end": v(-23.47, 0.51) * mm});
            skLineSegment(sketch, "E275", {"start": v(-23.47, 0.51) * mm, "end": v(-23.47, -0.28) * mm});
            skLineSegment(sketch, "E276", {"start": v(-23.47, -0.28) * mm, "end": v(-23.47, -1.39) * mm});
            skLineSegment(sketch, "E277", {"start": v(-23.47, -1.39) * mm, "end": v(-23.47, -2.66) * mm});
            skLineSegment(sketch, "E278", {"start": v(-23.47, -2.66) * mm, "end": v(-23.47, -3.94) * mm});
            skLineSegment(sketch, "E279", {"start": v(-23.47, -3.94) * mm, "end": v(-23.47, -5.05) * mm});
            skLineSegment(sketch, "E280", {"start": v(-23.47, -5.05) * mm, "end": v(-23.47, -5.84) * mm});
            skLineSegment(sketch, "E281", {"start": v(-23.47, -5.84) * mm, "end": v(-23.47, -6.14) * mm});
            skLineSegment(sketch, "E282", {"start": v(-23.47, -6.14) * mm, "end": v(-23.47, -6.21) * mm});
            skLineSegment(sketch, "E283", {"start": v(-23.47, -6.21) * mm, "end": v(-23.18, -6.85) * mm});
            skLineSegment(sketch, "E284", {"start": v(-23.18, -6.85) * mm, "end": v(-23.12, -6.9) * mm});
            skLineSegment(sketch, "E285", {"start": v(-23.12, -6.9) * mm, "end": v(-23.07, -6.95) * mm});
            skLineSegment(sketch, "E286", {"start": v(-23.07, -6.95) * mm, "end": v(-22.5, -7.2) * mm});
            skLineSegment(sketch, "E287", {"start": v(-22.5, -7.2) * mm, "end": v(-22.32, -7.2) * mm});
            skLineSegment(sketch, "E288", {"start": v(-22.32, -7.2) * mm, "end": v(-22.14, -7.2) * mm});
            skLineSegment(sketch, "E289", {"start": v(-22.14, -7.2) * mm, "end": v(-21.96, -7.2) * mm});
            skLineSegment(sketch, "E290", {"start": v(-21.96, -7.2) * mm, "end": v(-21.96, -7.31) * mm});
            skLineSegment(sketch, "E291", {"start": v(-21.96, -7.31) * mm, "end": v(-21.96, -7.42) * mm});
            skLineSegment(sketch, "E292", {"start": v(-21.96, -7.42) * mm, "end": v(-22.88, -7.42) * mm});
            skLineSegment(sketch, "E293", {"start": v(-22.88, -7.42) * mm, "end": v(-24.9, -7.42) * mm});
            skLineSegment(sketch, "E294", {"start": v(-24.9, -7.42) * mm, "end": v(-26.92, -7.42) * mm});
            skLineSegment(sketch, "E295", {"start": v(-26.92, -7.42) * mm, "end": v(-27.83, -7.42) * mm});
            skLineSegment(sketch, "E296", {"start": v(-27.83, -7.42) * mm, "end": v(-27.83, -7.31) * mm});
            skLineSegment(sketch, "E297", {"start": v(-27.83, -7.31) * mm, "end": v(-27.83, -7.2) * mm});
            skLineSegment(sketch, "E298", {"start": v(-27.83, -7.2) * mm, "end": v(-27.67, -7.2) * mm});
            skLineSegment(sketch, "E299", {"start": v(-27.67, -7.2) * mm, "end": v(-27.5, -7.2) * mm});
            skLineSegment(sketch, "E300", {"start": v(-27.5, -7.2) * mm, "end": v(-27.3, -7.2) * mm});
            skLineSegment(sketch, "E301", {"start": v(-27.3, -7.2) * mm, "end": v(-26.74, -6.95) * mm});
            skLineSegment(sketch, "E302", {"start": v(-26.74, -6.95) * mm, "end": v(-26.68, -6.9) * mm});
            skLineSegment(sketch, "E303", {"start": v(-26.68, -6.9) * mm, "end": v(-26.62, -6.85) * mm});
            skLineSegment(sketch, "E304", {"start": v(-26.62, -6.85) * mm, "end": v(-26.34, -6.32) * mm});
            skLineSegment(sketch, "E305", {"start": v(-26.34, -6.32) * mm, "end": v(-26.34, -6.14) * mm});
            skLineSegment(sketch, "E306", {"start": v(-26.34, -6.14) * mm, "end": v(-26.34, -5.74) * mm});
            skLineSegment(sketch, "E307", {"start": v(-26.34, -5.74) * mm, "end": v(-26.34, -4.7) * mm});
            skLineSegment(sketch, "E308", {"start": v(-26.34, -4.7) * mm, "end": v(-26.34, -3.22) * mm});
            skLineSegment(sketch, "E309", {"start": v(-26.34, -3.22) * mm, "end": v(-26.34, -1.52) * mm});
            skLineSegment(sketch, "E310", {"start": v(-26.34, -1.52) * mm, "end": v(-26.34, 0.17) * mm});
            skLineSegment(sketch, "E311", {"start": v(-26.34, 0.17) * mm, "end": v(-26.34, 1.65) * mm});
            skLineSegment(sketch, "E312", {"start": v(-26.34, 1.65) * mm, "end": v(-26.34, 2.7) * mm});
            skLineSegment(sketch, "E313", {"start": v(-26.34, 2.7) * mm, "end": v(-26.34, 3.1) * mm});
            skLineSegment(sketch, "E314", {"start": v(-26.34, 3.1) * mm, "end": v(-26.34, 3.61) * mm});
            skLineSegment(sketch, "E315", {"start": v(-26.34, 3.61) * mm, "end": v(-26.48, 5.04) * mm});
            skLineSegment(sketch, "E316", {"start": v(-26.48, 5.04) * mm, "end": v(-26.51, 5.17) * mm});
            skLineSegment(sketch, "E317", {"start": v(-26.51, 5.17) * mm, "end": v(-26.53, 5.32) * mm});
            skLineSegment(sketch, "E318", {"start": v(-26.53, 5.32) * mm, "end": v(-26.55, 5.47) * mm});
            skLineSegment(sketch, "E319", {"start": v(-26.55, 5.47) * mm, "end": v(-26.46, 5.46) * mm});
            skLineSegment(sketch, "E320", {"start": v(-26.46, 5.46) * mm, "end": v(-26.37, 5.45) * mm});
            skLineSegment(sketch, "E321", {"start": v(-26.37, 5.45) * mm, "end": v(-25.95, 5.08) * mm});
            skLineSegment(sketch, "E322", {"start": v(-25.95, 5.08) * mm, "end": v(-24.86, 4.13) * mm});
            skLineSegment(sketch, "E323", {"start": v(-24.86, 4.13) * mm, "end": v(-23.33, 2.77) * mm});
            skLineSegment(sketch, "E324", {"start": v(-23.33, 2.77) * mm, "end": v(-21.56, 1.22) * mm});
            skLineSegment(sketch, "E325", {"start": v(-21.56, 1.22) * mm, "end": v(-19.8, -0.34) * mm});
            skLineSegment(sketch, "E326", {"start": v(-19.8, -0.34) * mm, "end": v(-18.26, -1.69) * mm});
            skLineSegment(sketch, "E327", {"start": v(-18.26, -1.69) * mm, "end": v(-17.17, -2.65) * mm});
            skLineSegment(sketch, "E328", {"start": v(-17.17, -2.65) * mm, "end": v(-16.76, -3.01) * mm});
            skLineSegment(sketch, "E329", {"start": v(-16.76, -3.01) * mm, "end": v(-16.76, -2.71) * mm});
            skLineSegment(sketch, "E330", {"start": v(-16.76, -2.71) * mm, "end": v(-16.76, -1.93) * mm});
            skLineSegment(sketch, "E331", {"start": v(-16.76, -1.93) * mm, "end": v(-16.76, -0.83) * mm});
            skLineSegment(sketch, "E332", {"start": v(-16.76, -0.83) * mm, "end": v(-16.76, 0.44) * mm});
            skLineSegment(sketch, "E333", {"start": v(-16.76, 0.44) * mm, "end": v(-16.76, 1.7) * mm});
            skLineSegment(sketch, "E334", {"start": v(-16.76, 1.7) * mm, "end": v(-16.76, 2.81) * mm});
            skLineSegment(sketch, "E335", {"start": v(-16.76, 2.81) * mm, "end": v(-16.76, 3.6) * mm});
            skLineSegment(sketch, "E336", {"start": v(-16.76, 3.6) * mm, "end": v(-16.76, 3.9) * mm});
            skLineSegment(sketch, "E337", {"start": v(-16.76, 3.9) * mm, "end": v(-16.76, 4.08) * mm});
            skLineSegment(sketch, "E338", {"start": v(-16.76, 4.08) * mm, "end": v(-17.03, 4.6) * mm});
            skLineSegment(sketch, "E339", {"start": v(-17.03, 4.6) * mm, "end": v(-17.08, 4.66) * mm});
            skLineSegment(sketch, "E340", {"start": v(-17.08, 4.66) * mm, "end": v(-17.13, 4.7) * mm});
            skLineSegment(sketch, "E341", {"start": v(-17.13, 4.7) * mm, "end": v(-17.7, 4.96) * mm});
            skLineSegment(sketch, "E342", {"start": v(-17.7, 4.96) * mm, "end": v(-17.89, 4.96) * mm});
            skLineSegment(sketch, "E343", {"start": v(-17.89, 4.96) * mm, "end": v(-18.07, 4.96) * mm});
            skLineSegment(sketch, "E344", {"start": v(-18.07, 4.96) * mm, "end": v(-18.24, 4.96) * mm});
            skLineSegment(sketch, "E345", {"start": v(-18.24, 4.96) * mm, "end": v(-18.24, 5.07) * mm});
            skLineSegment(sketch, "E346", {"start": v(-18.24, 5.07) * mm, "end": v(-18.24, 5.17) * mm});
            skLineSegment(sketch, "E347", {"start": v(2.05, -7.2) * mm, "end": v(2.21, -7.2) * mm});
            skLineSegment(sketch, "E348", {"start": v(2.21, -7.2) * mm, "end": v(2.21, -7.31) * mm});
            skLineSegment(sketch, "E349", {"start": v(2.21, -7.31) * mm, "end": v(2.21, -7.42) * mm});
            skLineSegment(sketch, "E350", {"start": v(2.21, -7.42) * mm, "end": v(1.25, -7.42) * mm});
            skLineSegment(sketch, "E351", {"start": v(1.25, -7.42) * mm, "end": v(-0.87, -7.42) * mm});
            skLineSegment(sketch, "E352", {"start": v(-0.87, -7.42) * mm, "end": v(-3, -7.42) * mm});
            skLineSegment(sketch, "E353", {"start": v(-3, -7.42) * mm, "end": v(-3.96, -7.42) * mm});
            skLineSegment(sketch, "E354", {"start": v(-3.96, -7.42) * mm, "end": v(-3.96, -7.31) * mm});
            skLineSegment(sketch, "E355", {"start": v(-3.96, -7.31) * mm, "end": v(-3.96, -7.2) * mm});
            skLineSegment(sketch, "E356", {"start": v(-3.96, -7.2) * mm, "end": v(-3.79, -7.2) * mm});
            skLineSegment(sketch, "E357", {"start": v(-3.79, -7.2) * mm, "end": v(-3.64, -7.2) * mm});
            skLineSegment(sketch, "E358", {"start": v(-3.64, -7.2) * mm, "end": v(-3.21, -7) * mm});
            skLineSegment(sketch, "E359", {"start": v(-3.21, -7) * mm, "end": v(-3.18, -6.96) * mm});
            skLineSegment(sketch, "E360", {"start": v(-3.18, -6.96) * mm, "end": v(-3.15, -6.91) * mm});
            skLineSegment(sketch, "E361", {"start": v(-3.15, -6.91) * mm, "end": v(-3, -6.6) * mm});
            skLineSegment(sketch, "E362", {"start": v(-3, -6.6) * mm, "end": v(-3, -6.5) * mm});
            skLineSegment(sketch, "E363", {"start": v(-3, -6.5) * mm, "end": v(-3, -6.38) * mm});
            skLineSegment(sketch, "E364", {"start": v(-3, -6.38) * mm, "end": v(-3.06, -6.1) * mm});
            skLineSegment(sketch, "E365", {"start": v(-3.06, -6.1) * mm, "end": v(-3.07, -6.05) * mm});
            skLineSegment(sketch, "E366", {"start": v(-3.07, -6.05) * mm, "end": v(-3.2, -5.75) * mm});
            skLineSegment(sketch, "E367", {"start": v(-3.2, -5.75) * mm, "end": v(-3.48, -5.09) * mm});
            skLineSegment(sketch, "E368", {"start": v(-3.48, -5.09) * mm, "end": v(-3.76, -4.42) * mm});
            skLineSegment(sketch, "E369", {"start": v(-3.76, -4.42) * mm, "end": v(-3.9, -4.12) * mm});
            skLineSegment(sketch, "E370", {"start": v(-3.9, -4.12) * mm, "end": v(-4.08, -4.12) * mm});
            skLineSegment(sketch, "E371", {"start": v(-4.08, -4.12) * mm, "end": v(-4.59, -4.12) * mm});
            skLineSegment(sketch, "E372", {"start": v(-4.59, -4.12) * mm, "end": v(-5.3, -4.12) * mm});
            skLineSegment(sketch, "E373", {"start": v(-5.3, -4.12) * mm, "end": v(-6.12, -4.12) * mm});
            skLineSegment(sketch, "E374", {"start": v(-6.12, -4.12) * mm, "end": v(-6.93, -4.12) * mm});
            skLineSegment(sketch, "E375", {"start": v(-6.93, -4.12) * mm, "end": v(-7.65, -4.12) * mm});
            skLineSegment(sketch, "E376", {"start": v(-7.65, -4.12) * mm, "end": v(-8.15, -4.12) * mm});
            skLineSegment(sketch, "E377", {"start": v(-8.15, -4.12) * mm, "end": v(-8.34, -4.12) * mm});
            skLineSegment(sketch, "E378", {"start": v(-8.34, -4.12) * mm, "end": v(-8.47, -4.43) * mm});
            skLineSegment(sketch, "E379", {"start": v(-8.47, -4.43) * mm, "end": v(-8.76, -5.1) * mm});
            skLineSegment(sketch, "E380", {"start": v(-8.76, -5.1) * mm, "end": v(-9.05, -5.77) * mm});
            skLineSegment(sketch, "E381", {"start": v(-9.05, -5.77) * mm, "end": v(-9.18, -6.07) * mm});
            skLineSegment(sketch, "E382", {"start": v(-9.18, -6.07) * mm, "end": v(-9.2, -6.1) * mm});
            skLineSegment(sketch, "E383", {"start": v(-9.2, -6.1) * mm, "end": v(-9.26, -6.4) * mm});
            skLineSegment(sketch, "E384", {"start": v(-9.26, -6.4) * mm, "end": v(-9.26, -6.5) * mm});
            skLineSegment(sketch, "E385", {"start": v(-9.26, -6.5) * mm, "end": v(-9.26, -6.62) * mm});
            skLineSegment(sketch, "E386", {"start": v(-9.26, -6.62) * mm, "end": v(-9.1, -6.93) * mm});
            skLineSegment(sketch, "E387", {"start": v(-9.1, -6.93) * mm, "end": v(-9.06, -6.97) * mm});
            skLineSegment(sketch, "E388", {"start": v(-9.06, -6.97) * mm, "end": v(-9.03, -7) * mm});
            skLineSegment(sketch, "E389", {"start": v(-9.03, -7) * mm, "end": v(-8.6, -7.2) * mm});
            skLineSegment(sketch, "E390", {"start": v(-8.6, -7.2) * mm, "end": v(-8.45, -7.2) * mm});
            skLineSegment(sketch, "E391", {"start": v(-8.45, -7.2) * mm, "end": v(-8.28, -7.2) * mm});
            skLineSegment(sketch, "E392", {"start": v(-8.28, -7.2) * mm, "end": v(-8.28, -7.31) * mm});
            skLineSegment(sketch, "E393", {"start": v(-8.28, -7.31) * mm, "end": v(-8.28, -7.42) * mm});
            skLineSegment(sketch, "E394", {"start": v(-8.28, -7.42) * mm, "end": v(-8.46, -7.42) * mm});
            skLineSegment(sketch, "E395", {"start": v(-8.46, -7.42) * mm, "end": v(-8.93, -7.42) * mm});
            skLineSegment(sketch, "E396", {"start": v(-8.93, -7.42) * mm, "end": v(-9.6, -7.42) * mm});
            skLineSegment(sketch, "E397", {"start": v(-9.6, -7.42) * mm, "end": v(-10.38, -7.42) * mm});
            skLineSegment(sketch, "E398", {"start": v(-10.38, -7.42) * mm, "end": v(-11.15, -7.42) * mm});
            skLineSegment(sketch, "E399", {"start": v(-11.15, -7.42) * mm, "end": v(-11.82, -7.42) * mm});
            skLineSegment(sketch, "E400", {"start": v(-11.82, -7.42) * mm, "end": v(-12.3, -7.42) * mm});
            skLineSegment(sketch, "E401", {"start": v(-12.3, -7.42) * mm, "end": v(-12.47, -7.42) * mm});
            skLineSegment(sketch, "E402", {"start": v(-12.47, -7.42) * mm, "end": v(-12.47, -7.31) * mm});
            skLineSegment(sketch, "E403", {"start": v(-12.47, -7.31) * mm, "end": v(-12.47, -7.2) * mm});
            skLineSegment(sketch, "E404", {"start": v(-12.47, -7.2) * mm, "end": v(-12.3, -7.2) * mm});
            skLineSegment(sketch, "E405", {"start": v(-12.3, -7.2) * mm, "end": v(-12.09, -7.2) * mm});
            skLineSegment(sketch, "E406", {"start": v(-12.09, -7.2) * mm, "end": v(-11.5, -6.98) * mm});
            skLineSegment(sketch, "E407", {"start": v(-11.5, -6.98) * mm, "end": v(-11.43, -6.93) * mm});
            skLineSegment(sketch, "E408", {"start": v(-11.43, -6.93) * mm, "end": v(-11.35, -6.89) * mm});
            skLineSegment(sketch, "E409", {"start": v(-11.35, -6.89) * mm, "end": v(-10.76, -6.2) * mm});
            skLineSegment(sketch, "E410", {"start": v(-10.76, -6.2) * mm, "end": v(-10.71, -6.12) * mm});
            skLineSegment(sketch, "E411", {"start": v(-10.71, -6.12) * mm, "end": v(-10.53, -5.72) * mm});
            skLineSegment(sketch, "E412", {"start": v(-10.53, -5.72) * mm, "end": v(-10.03, -4.66) * mm});
            skLineSegment(sketch, "E413", {"start": v(-10.03, -4.66) * mm, "end": v(-9.34, -3.17) * mm});
            skLineSegment(sketch, "E414", {"start": v(-9.34, -3.17) * mm, "end": v(-8.54, -1.46) * mm});
            skLineSegment(sketch, "E415", {"start": v(-8.54, -1.46) * mm, "end": v(-7.74, 0.25) * mm});
            skLineSegment(sketch, "E416", {"start": v(-7.74, 0.25) * mm, "end": v(-7.05, 1.74) * mm});
            skLineSegment(sketch, "E417", {"start": v(-7.05, 1.74) * mm, "end": v(-6.55, 2.8) * mm});
            skLineSegment(sketch, "E418", {"start": v(-6.55, 2.8) * mm, "end": v(-6.37, 3.2) * mm});
            skLineSegment(sketch, "E419", {"start": v(-6.37, 3.2) * mm, "end": v(-6.26, 3.43) * mm});
            skLineSegment(sketch, "E420", {"start": v(-6.26, 3.43) * mm, "end": v(-5.96, 4.14) * mm});
            skLineSegment(sketch, "E421", {"start": v(-5.96, 4.14) * mm, "end": v(-5.67, 4.88) * mm});
            skLineSegment(sketch, "E422", {"start": v(-5.67, 4.88) * mm, "end": v(-5.48, 5.42) * mm});
            skLineSegment(sketch, "E423", {"start": v(-5.48, 5.42) * mm, "end": v(-5.4, 5.68) * mm});
            skLineSegment(sketch, "E424", {"start": v(-5.4, 5.68) * mm, "end": v(-5.4, 5.76) * mm});
            skLineSegment(sketch, "E425", {"start": v(-5.4, 5.76) * mm, "end": v(-5.21, 5.76) * mm});
            skLineSegment(sketch, "E426", {"start": v(-5.21, 5.76) * mm, "end": v(-4.97, 5.25) * mm});
            skLineSegment(sketch, "E427", {"start": v(-4.97, 5.25) * mm, "end": v(-4.34, 3.92) * mm});
            skLineSegment(sketch, "E428", {"start": v(-4.34, 3.92) * mm, "end": v(-3.44, 2.03) * mm});
            skLineSegment(sketch, "E429", {"start": v(-3.44, 2.03) * mm, "end": v(-2.4, -0.14) * mm});
            skLineSegment(sketch, "E430", {"start": v(-2.4, -0.14) * mm, "end": v(-1.37, -2.3) * mm});
            skLineSegment(sketch, "E431", {"start": v(-1.37, -2.3) * mm, "end": v(-0.47, -4.19) * mm});
            skLineSegment(sketch, "E432", {"start": v(-0.47, -4.19) * mm, "end": v(0.17, -5.53) * mm});
            skLineSegment(sketch, "E433", {"start": v(0.17, -5.53) * mm, "end": v(0.4, -6.03) * mm});
            skLineSegment(sketch, "E434", {"start": v(0.4, -6.03) * mm, "end": v(0.45, -6.13) * mm});
            skLineSegment(sketch, "E435", {"start": v(0.45, -6.13) * mm, "end": v(1.06, -6.88) * mm});
            skLineSegment(sketch, "E436", {"start": v(1.06, -6.88) * mm, "end": v(1.13, -6.92) * mm});
            skLineSegment(sketch, "E437", {"start": v(1.13, -6.92) * mm, "end": v(1.2, -6.97) * mm});
            skLineSegment(sketch, "E438", {"start": v(1.2, -6.97) * mm, "end": v(1.84, -7.2) * mm});
            skLineSegment(sketch, "E439", {"start": v(1.84, -7.2) * mm, "end": v(2.05, -7.2) * mm});
            skLineSegment(sketch, "E440", {"start": v(-7.98, -3.3) * mm, "end": v(-7.82, -3.3) * mm});
            skLineSegment(sketch, "E441", {"start": v(-7.82, -3.3) * mm, "end": v(-7.4, -3.3) * mm});
            skLineSegment(sketch, "E442", {"start": v(-7.4, -3.3) * mm, "end": v(-6.8, -3.3) * mm});
            skLineSegment(sketch, "E443", {"start": v(-6.8, -3.3) * mm, "end": v(-6.12, -3.3) * mm});
            skLineSegment(sketch, "E444", {"start": v(-6.12, -3.3) * mm, "end": v(-5.43, -3.3) * mm});
            skLineSegment(sketch, "E445", {"start": v(-5.43, -3.3) * mm, "end": v(-4.83, -3.3) * mm});
            skLineSegment(sketch, "E446", {"start": v(-4.83, -3.3) * mm, "end": v(-4.41, -3.3) * mm});
            skLineSegment(sketch, "E447", {"start": v(-4.41, -3.3) * mm, "end": v(-4.25, -3.3) * mm});
            skLineSegment(sketch, "E448", {"start": v(-4.25, -3.3) * mm, "end": v(-4.33, -3.12) * mm});
            skLineSegment(sketch, "E449", {"start": v(-4.33, -3.12) * mm, "end": v(-4.54, -2.62) * mm});
            skLineSegment(sketch, "E450", {"start": v(-4.54, -2.62) * mm, "end": v(-4.83, -1.92) * mm});
            skLineSegment(sketch, "E451", {"start": v(-4.83, -1.92) * mm, "end": v(-5.17, -1.11) * mm});
            skLineSegment(sketch, "E452", {"start": v(-5.17, -1.11) * mm, "end": v(-5.51, -0.3) * mm});
            skLineSegment(sketch, "E453", {"start": v(-5.51, -0.3) * mm, "end": v(-5.8, 0.4) * mm});
            skLineSegment(sketch, "E454", {"start": v(-5.8, 0.4) * mm, "end": v(-6.02, 0.9) * mm});
            skLineSegment(sketch, "E455", {"start": v(-6.02, 0.9) * mm, "end": v(-6.1, 1.08) * mm});
            skLineSegment(sketch, "E456", {"start": v(-6.1, 1.08) * mm, "end": v(-6.18, 0.9) * mm});
            skLineSegment(sketch, "E457", {"start": v(-6.18, 0.9) * mm, "end": v(-6.4, 0.4) * mm});
            skLineSegment(sketch, "E458", {"start": v(-6.4, 0.4) * mm, "end": v(-6.7, -0.3) * mm});
            skLineSegment(sketch, "E459", {"start": v(-6.7, -0.3) * mm, "end": v(-7.04, -1.11) * mm});
            skLineSegment(sketch, "E460", {"start": v(-7.04, -1.11) * mm, "end": v(-7.39, -1.92) * mm});
            skLineSegment(sketch, "E461", {"start": v(-7.39, -1.92) * mm, "end": v(-7.69, -2.62) * mm});
            skLineSegment(sketch, "E462", {"start": v(-7.69, -2.62) * mm, "end": v(-7.9, -3.12) * mm});
            skLineSegment(sketch, "E463", {"start": v(-7.9, -3.12) * mm, "end": v(-7.98, -3.3) * mm});
            skLineSegment(sketch, "E464", {"start": v(12.7, 2.05) * mm, "end": v(12.7, 1.7) * mm});
            skLineSegment(sketch, "E465", {"start": v(12.7, 1.7) * mm, "end": v(12.42, 0.78) * mm});
            skLineSegment(sketch, "E466", {"start": v(12.42, 0.78) * mm, "end": v(12.37, 0.68) * mm});
            skLineSegment(sketch, "E467", {"start": v(12.37, 0.68) * mm, "end": v(12.26, 0.5) * mm});
            skLineSegment(sketch, "E468", {"start": v(12.26, 0.5) * mm, "end": v(11.55, -0.2) * mm});
            skLineSegment(sketch, "E469", {"start": v(11.55, -0.2) * mm, "end": v(10.62, -0.54) * mm});
            skLineSegment(sketch, "E470", {"start": v(10.62, -0.54) * mm, "end": v(10.4, -0.56) * mm});
            skLineSegment(sketch, "E471", {"start": v(10.4, -0.56) * mm, "end": v(10.63, -0.57) * mm});
            skLineSegment(sketch, "E472", {"start": v(10.63, -0.57) * mm, "end": v(11.69, -0.86) * mm});
            skLineSegment(sketch, "E473", {"start": v(11.69, -0.86) * mm, "end": v(12.59, -1.4) * mm});
            skLineSegment(sketch, "E474", {"start": v(12.59, -1.4) * mm, "end": v(12.75, -1.55) * mm});
            skLineSegment(sketch, "E475", {"start": v(12.75, -1.55) * mm, "end": v(12.9, -1.7) * mm});
            skLineSegment(sketch, "E476", {"start": v(12.9, -1.7) * mm, "end": v(13.45, -2.57) * mm});
            skLineSegment(sketch, "E477", {"start": v(13.45, -2.57) * mm, "end": v(13.7, -3.51) * mm});
            skLineSegment(sketch, "E478", {"start": v(13.7, -3.51) * mm, "end": v(13.7, -3.83) * mm});
            skLineSegment(sketch, "E479", {"start": v(13.7, -3.83) * mm, "end": v(13.7, -4.14) * mm});
            skLineSegment(sketch, "E480", {"start": v(13.7, -4.14) * mm, "end": v(13.49, -5.06) * mm});
            skLineSegment(sketch, "E481", {"start": v(13.49, -5.06) * mm, "end": v(12.88, -6.03) * mm});
            skLineSegment(sketch, "E482", {"start": v(12.88, -6.03) * mm, "end": v(11.86, -6.76) * mm});
            skLineSegment(sketch, "E483", {"start": v(11.86, -6.76) * mm, "end": v(10.8, -7.15) * mm});
            skLineSegment(sketch, "E484", {"start": v(10.8, -7.15) * mm, "end": v(10.44, -7.23) * mm});
            skLineSegment(sketch, "E485", {"start": v(10.44, -7.23) * mm, "end": v(10.29, -7.26) * mm});
            skLineSegment(sketch, "E486", {"start": v(10.29, -7.26) * mm, "end": v(8.89, -7.42) * mm});
            skLineSegment(sketch, "E487", {"start": v(8.89, -7.42) * mm, "end": v(8.42, -7.42) * mm});
            skLineSegment(sketch, "E488", {"start": v(8.42, -7.42) * mm, "end": v(7.47, -7.42) * mm});
            skLineSegment(sketch, "E489", {"start": v(7.47, -7.42) * mm, "end": v(5.38, -7.42) * mm});
            skLineSegment(sketch, "E490", {"start": v(5.38, -7.42) * mm, "end": v(3.3, -7.42) * mm});
            skLineSegment(sketch, "E491", {"start": v(3.3, -7.42) * mm, "end": v(2.34, -7.42) * mm});
            skLineSegment(sketch, "E492", {"start": v(2.34, -7.42) * mm, "end": v(2.34, -7.31) * mm});
            skLineSegment(sketch, "E493", {"start": v(2.34, -7.31) * mm, "end": v(2.34, -7.2) * mm});
            skLineSegment(sketch, "E494", {"start": v(2.34, -7.2) * mm, "end": v(2.45, -7.2) * mm});
            skLineSegment(sketch, "E495", {"start": v(2.45, -7.2) * mm, "end": v(2.57, -7.2) * mm});
            skLineSegment(sketch, "E496", {"start": v(2.57, -7.2) * mm, "end": v(2.77, -7.2) * mm});
            skLineSegment(sketch, "E497", {"start": v(2.77, -7.2) * mm, "end": v(3.32, -6.94) * mm});
            skLineSegment(sketch, "E498", {"start": v(3.32, -6.94) * mm, "end": v(3.38, -6.9) * mm});
            skLineSegment(sketch, "E499", {"start": v(3.38, -6.9) * mm, "end": v(3.43, -6.84) * mm});
            skLineSegment(sketch, "E500", {"start": v(3.43, -6.84) * mm, "end": v(3.72, -6.18) * mm});
            skLineSegment(sketch, "E501", {"start": v(3.72, -6.18) * mm, "end": v(3.72, -6.1) * mm});
            skLineSegment(sketch, "E502", {"start": v(3.72, -6.1) * mm, "end": v(3.72, -5.67) * mm});
            skLineSegment(sketch, "E503", {"start": v(3.72, -5.67) * mm, "end": v(3.72, -4.54) * mm});
            skLineSegment(sketch, "E504", {"start": v(3.72, -4.54) * mm, "end": v(3.72, -2.95) * mm});
            skLineSegment(sketch, "E505", {"start": v(3.72, -2.95) * mm, "end": v(3.72, -1.12) * mm});
            skLineSegment(sketch, "E506", {"start": v(3.72, -1.12) * mm, "end": v(3.72, 0.7) * mm});
            skLineSegment(sketch, "E507", {"start": v(3.72, 0.7) * mm, "end": v(3.72, 2.3) * mm});
            skLineSegment(sketch, "E508", {"start": v(3.72, 2.3) * mm, "end": v(3.72, 3.42) * mm});
            skLineSegment(sketch, "E509", {"start": v(3.72, 3.42) * mm, "end": v(3.72, 3.85) * mm});
            skLineSegment(sketch, "E510", {"start": v(3.72, 3.85) * mm, "end": v(3.72, 3.98) * mm});
            skLineSegment(sketch, "E511", {"start": v(3.72, 3.98) * mm, "end": v(3.54, 4.49) * mm});
            skLineSegment(sketch, "E512", {"start": v(3.54, 4.49) * mm, "end": v(3.13, 4.83) * mm});
            skLineSegment(sketch, "E513", {"start": v(3.13, 4.83) * mm, "end": v(3.01, 4.88) * mm});
            skLineSegment(sketch, "E514", {"start": v(3.01, 4.88) * mm, "end": v(2.98, 4.9) * mm});
            skLineSegment(sketch, "E515", {"start": v(2.98, 4.9) * mm, "end": v(2.67, 4.96) * mm});
            skLineSegment(sketch, "E516", {"start": v(2.67, 4.96) * mm, "end": v(2.57, 4.96) * mm});
            skLineSegment(sketch, "E517", {"start": v(2.57, 4.96) * mm, "end": v(2.45, 4.96) * mm});
            skLineSegment(sketch, "E518", {"start": v(2.45, 4.96) * mm, "end": v(2.34, 4.96) * mm});
            skLineSegment(sketch, "E519", {"start": v(2.34, 4.96) * mm, "end": v(2.34, 5.07) * mm});
            skLineSegment(sketch, "E520", {"start": v(2.34, 5.07) * mm, "end": v(2.34, 5.17) * mm});
            skLineSegment(sketch, "E521", {"start": v(2.34, 5.17) * mm, "end": v(3.22, 5.17) * mm});
            skLineSegment(sketch, "E522", {"start": v(3.22, 5.17) * mm, "end": v(5.15, 5.17) * mm});
            skLineSegment(sketch, "E523", {"start": v(5.15, 5.17) * mm, "end": v(7.08, 5.17) * mm});
            skLineSegment(sketch, "E524", {"start": v(7.08, 5.17) * mm, "end": v(7.96, 5.17) * mm});
            skLineSegment(sketch, "E525", {"start": v(7.96, 5.17) * mm, "end": v(8.48, 5.17) * mm});
            skLineSegment(sketch, "E526", {"start": v(8.48, 5.17) * mm, "end": v(10.04, 4.98) * mm});
            skLineSegment(sketch, "E527", {"start": v(10.04, 4.98) * mm, "end": v(11.52, 4.4) * mm});
            skLineSegment(sketch, "E528", {"start": v(11.52, 4.4) * mm, "end": v(12.4, 3.41) * mm});
            skLineSegment(sketch, "E529", {"start": v(12.4, 3.41) * mm, "end": v(12.7, 2.39) * mm});
            skLineSegment(sketch, "E530", {"start": v(12.7, 2.39) * mm, "end": v(12.7, 2.05) * mm});
            skLineSegment(sketch, "E531", {"start": v(10.3, -3.64) * mm, "end": v(10.3, -3.42) * mm});
            skLineSegment(sketch, "E532", {"start": v(10.3, -3.42) * mm, "end": v(10.2, -2.75) * mm});
            skLineSegment(sketch, "E533", {"start": v(10.2, -2.75) * mm, "end": v(9.96, -2.13) * mm});
            skLineSegment(sketch, "E534", {"start": v(9.96, -2.13) * mm, "end": v(9.9, -2.02) * mm});
            skLineSegment(sketch, "E535", {"start": v(9.9, -2.02) * mm, "end": v(9.77, -1.82) * mm});
            skLineSegment(sketch, "E536", {"start": v(9.77, -1.82) * mm, "end": v(8.9, -1.08) * mm});
            skLineSegment(sketch, "E537", {"start": v(8.9, -1.08) * mm, "end": v(7.74, -0.77) * mm});
            skLineSegment(sketch, "E538", {"start": v(7.74, -0.77) * mm, "end": v(7.35, -0.77) * mm});
            skLineSegment(sketch, "E539", {"start": v(7.35, -0.77) * mm, "end": v(7.34, -0.77) * mm});
            skLineSegment(sketch, "E540", {"start": v(7.34, -0.77) * mm, "end": v(7.32, -0.77) * mm});
            skLineSegment(sketch, "E541", {"start": v(7.32, -0.77) * mm, "end": v(7.31, -0.77) * mm});
            skLineSegment(sketch, "E542", {"start": v(7.31, -0.77) * mm, "end": v(7.31, -0.58) * mm});
            skLineSegment(sketch, "E543", {"start": v(7.31, -0.58) * mm, "end": v(7.54, -0.58) * mm});
            skLineSegment(sketch, "E544", {"start": v(7.54, -0.58) * mm, "end": v(8.22, -0.43) * mm});
            skLineSegment(sketch, "E545", {"start": v(8.22, -0.43) * mm, "end": v(8.84, -0.09) * mm});
            skLineSegment(sketch, "E546", {"start": v(8.84, -0.09) * mm, "end": v(8.95, 0.01) * mm});
            skLineSegment(sketch, "E547", {"start": v(8.95, 0.01) * mm, "end": v(9.05, 0.1) * mm});
            skLineSegment(sketch, "E548", {"start": v(9.05, 0.1) * mm, "end": v(9.42, 0.76) * mm});
            skLineSegment(sketch, "E549", {"start": v(9.42, 0.76) * mm, "end": v(9.58, 1.57) * mm});
            skLineSegment(sketch, "E550", {"start": v(9.58, 1.57) * mm, "end": v(9.58, 1.84) * mm});
            skLineSegment(sketch, "E551", {"start": v(9.58, 1.84) * mm, "end": v(9.58, 2.11) * mm});
            skLineSegment(sketch, "E552", {"start": v(9.58, 2.11) * mm, "end": v(9.44, 2.94) * mm});
            skLineSegment(sketch, "E553", {"start": v(9.44, 2.94) * mm, "end": v(9, 3.72) * mm});
            skLineSegment(sketch, "E554", {"start": v(9, 3.72) * mm, "end": v(8.3, 4.2) * mm});
            skLineSegment(sketch, "E555", {"start": v(8.3, 4.2) * mm, "end": v(7.54, 4.35) * mm});
            skLineSegment(sketch, "E556", {"start": v(7.54, 4.35) * mm, "end": v(7.3, 4.35) * mm});
            skLineSegment(sketch, "E557", {"start": v(7.3, 4.35) * mm, "end": v(7, 4.35) * mm});
            skLineSegment(sketch, "E558", {"start": v(7, 4.35) * mm, "end": v(6.7, 4.35) * mm});
            skLineSegment(sketch, "E559", {"start": v(6.7, 4.35) * mm, "end": v(6.7, 3.89) * mm});
            skLineSegment(sketch, "E560", {"start": v(6.7, 3.89) * mm, "end": v(6.7, 2.65) * mm});
            skLineSegment(sketch, "E561", {"start": v(6.7, 2.65) * mm, "end": v(6.7, 0.9) * mm});
            skLineSegment(sketch, "E562", {"start": v(6.7, 0.9) * mm, "end": v(6.7, -1.11) * mm});
            skLineSegment(sketch, "E563", {"start": v(6.7, -1.11) * mm, "end": v(6.7, -3.12) * mm});
            skLineSegment(sketch, "E564", {"start": v(6.7, -3.12) * mm, "end": v(6.7, -4.87) * mm});
            skLineSegment(sketch, "E565", {"start": v(6.7, -4.87) * mm, "end": v(6.7, -6.1) * mm});
            skLineSegment(sketch, "E566", {"start": v(6.7, -6.1) * mm, "end": v(6.7, -6.58) * mm});
            skLineSegment(sketch, "E567", {"start": v(6.7, -6.58) * mm, "end": v(6.83, -6.58) * mm});
            skLineSegment(sketch, "E568", {"start": v(6.83, -6.58) * mm, "end": v(7.12, -6.58) * mm});
            skLineSegment(sketch, "E569", {"start": v(7.12, -6.58) * mm, "end": v(7.41, -6.58) * mm});
            skLineSegment(sketch, "E570", {"start": v(7.41, -6.58) * mm, "end": v(7.54, -6.58) * mm});
            skLineSegment(sketch, "E571", {"start": v(7.54, -6.58) * mm, "end": v(7.82, -6.58) * mm});
            skLineSegment(sketch, "E572", {"start": v(7.82, -6.58) * mm, "end": v(8.65, -6.4) * mm});
            skLineSegment(sketch, "E573", {"start": v(8.65, -6.4) * mm, "end": v(9.4, -5.98) * mm});
            skLineSegment(sketch, "E574", {"start": v(9.4, -5.98) * mm, "end": v(9.53, -5.86) * mm});
            skLineSegment(sketch, "E575", {"start": v(9.53, -5.86) * mm, "end": v(9.65, -5.75) * mm});
            skLineSegment(sketch, "E576", {"start": v(9.65, -5.75) * mm, "end": v(10.1, -4.95) * mm});
            skLineSegment(sketch, "E577", {"start": v(10.1, -4.95) * mm, "end": v(10.3, -3.97) * mm});
            skLineSegment(sketch, "E578", {"start": v(10.3, -3.97) * mm, "end": v(10.3, -3.64) * mm});
            skLineSegment(sketch, "E579", {"start": v(24.85, -7.42) * mm, "end": v(24.43, -7.42) * mm});
            skLineSegment(sketch, "E580", {"start": v(24.43, -7.42) * mm, "end": v(23.3, -7.42) * mm});
            skLineSegment(sketch, "E581", {"start": v(23.3, -7.42) * mm, "end": v(21.73, -7.42) * mm});
            skLineSegment(sketch, "E582", {"start": v(21.73, -7.42) * mm, "end": v(19.91, -7.42) * mm});
            skLineSegment(sketch, "E583", {"start": v(19.91, -7.42) * mm, "end": v(18.1, -7.42) * mm});
            skLineSegment(sketch, "E584", {"start": v(18.1, -7.42) * mm, "end": v(16.51, -7.42) * mm});
            skLineSegment(sketch, "E585", {"start": v(16.51, -7.42) * mm, "end": v(15.4, -7.42) * mm});
            skLineSegment(sketch, "E586", {"start": v(15.4, -7.42) * mm, "end": v(14.97, -7.42) * mm});
            skLineSegment(sketch, "E587", {"start": v(14.97, -7.42) * mm, "end": v(14.97, -7.31) * mm});
            skLineSegment(sketch, "E588", {"start": v(14.97, -7.31) * mm, "end": v(14.97, -7.2) * mm});
            skLineSegment(sketch, "E589", {"start": v(14.97, -7.2) * mm, "end": v(15.1, -7.2) * mm});
            skLineSegment(sketch, "E590", {"start": v(15.1, -7.2) * mm, "end": v(15.22, -7.2) * mm});
            skLineSegment(sketch, "E591", {"start": v(15.22, -7.2) * mm, "end": v(15.42, -7.2) * mm});
            skLineSegment(sketch, "E592", {"start": v(15.42, -7.2) * mm, "end": v(15.98, -6.94) * mm});
            skLineSegment(sketch, "E593", {"start": v(15.98, -6.94) * mm, "end": v(16.03, -6.9) * mm});
            skLineSegment(sketch, "E594", {"start": v(16.03, -6.9) * mm, "end": v(16.09, -6.84) * mm});
            skLineSegment(sketch, "E595", {"start": v(16.09, -6.84) * mm, "end": v(16.37, -6.2) * mm});
            skLineSegment(sketch, "E596", {"start": v(16.37, -6.2) * mm, "end": v(16.38, -6.12) * mm});
            skLineSegment(sketch, "E597", {"start": v(16.38, -6.12) * mm, "end": v(16.38, -5.69) * mm});
            skLineSegment(sketch, "E598", {"start": v(16.38, -5.69) * mm, "end": v(16.38, -4.56) * mm});
            skLineSegment(sketch, "E599", {"start": v(16.38, -4.56) * mm, "end": v(16.38, -2.95) * mm});
            skLineSegment(sketch, "E600", {"start": v(16.38, -2.95) * mm, "end": v(16.38, -1.12) * mm});
            skLineSegment(sketch, "E601", {"start": v(16.38, -1.12) * mm, "end": v(16.38, 0.71) * mm});
            skLineSegment(sketch, "E602", {"start": v(16.38, 0.71) * mm, "end": v(16.38, 2.31) * mm});
            skLineSegment(sketch, "E603", {"start": v(16.38, 2.31) * mm, "end": v(16.38, 3.44) * mm});
            skLineSegment(sketch, "E604", {"start": v(16.38, 3.44) * mm, "end": v(16.38, 3.87) * mm});
            skLineSegment(sketch, "E605", {"start": v(16.38, 3.87) * mm, "end": v(16.37, 3.95) * mm});
            skLineSegment(sketch, "E606", {"start": v(16.37, 3.95) * mm, "end": v(16.09, 4.6) * mm});
            skLineSegment(sketch, "E607", {"start": v(16.09, 4.6) * mm, "end": v(16.03, 4.65) * mm});
            skLineSegment(sketch, "E608", {"start": v(16.03, 4.65) * mm, "end": v(15.98, 4.7) * mm});
            skLineSegment(sketch, "E609", {"start": v(15.98, 4.7) * mm, "end": v(15.41, 4.96) * mm});
            skLineSegment(sketch, "E610", {"start": v(15.41, 4.96) * mm, "end": v(15.22, 4.96) * mm});
            skLineSegment(sketch, "E611", {"start": v(15.22, 4.96) * mm, "end": v(15.1, 4.96) * mm});
            skLineSegment(sketch, "E612", {"start": v(15.1, 4.96) * mm, "end": v(14.97, 4.96) * mm});
            skLineSegment(sketch, "E613", {"start": v(14.97, 4.96) * mm, "end": v(14.97, 5.07) * mm});
            skLineSegment(sketch, "E614", {"start": v(14.97, 5.07) * mm, "end": v(14.97, 5.17) * mm});
            skLineSegment(sketch, "E615", {"start": v(14.97, 5.17) * mm, "end": v(15.29, 5.17) * mm});
            skLineSegment(sketch, "E616", {"start": v(15.29, 5.17) * mm, "end": v(16.12, 5.17) * mm});
            skLineSegment(sketch, "E617", {"start": v(16.12, 5.17) * mm, "end": v(17.3, 5.17) * mm});
            skLineSegment(sketch, "E618", {"start": v(17.3, 5.17) * mm, "end": v(18.66, 5.17) * mm});
            skLineSegment(sketch, "E619", {"start": v(18.66, 5.17) * mm, "end": v(20.02, 5.17) * mm});
            skLineSegment(sketch, "E620", {"start": v(20.02, 5.17) * mm, "end": v(21.2, 5.17) * mm});
            skLineSegment(sketch, "E621", {"start": v(21.2, 5.17) * mm, "end": v(22.04, 5.17) * mm});
            skLineSegment(sketch, "E622", {"start": v(22.04, 5.17) * mm, "end": v(22.36, 5.17) * mm});
            skLineSegment(sketch, "E623", {"start": v(22.36, 5.17) * mm, "end": v(22.67, 5.17) * mm});
            skLineSegment(sketch, "E624", {"start": v(22.67, 5.17) * mm, "end": v(23.48, 5.26) * mm});
            skLineSegment(sketch, "E625", {"start": v(23.48, 5.26) * mm, "end": v(23.6, 5.28) * mm});
            skLineSegment(sketch, "E626", {"start": v(23.6, 5.28) * mm, "end": v(23.7, 5.3) * mm});
            skLineSegment(sketch, "E627", {"start": v(23.7, 5.3) * mm, "end": v(24.5, 5.47) * mm});
            skLineSegment(sketch, "E628", {"start": v(24.5, 5.47) * mm, "end": v(24.54, 5.49) * mm});
            skLineSegment(sketch, "E629", {"start": v(24.54, 5.49) * mm, "end": v(24.54, 5.34) * mm});
            skLineSegment(sketch, "E630", {"start": v(24.54, 5.34) * mm, "end": v(24.54, 4.97) * mm});
            skLineSegment(sketch, "E631", {"start": v(24.54, 4.97) * mm, "end": v(24.54, 4.43) * mm});
            skLineSegment(sketch, "E632", {"start": v(24.54, 4.43) * mm, "end": v(24.54, 3.82) * mm});
            skLineSegment(sketch, "E633", {"start": v(24.54, 3.82) * mm, "end": v(24.54, 3.2) * mm});
            skLineSegment(sketch, "E634", {"start": v(24.54, 3.2) * mm, "end": v(24.54, 2.67) * mm});
            skLineSegment(sketch, "E635", {"start": v(24.54, 2.67) * mm, "end": v(24.54, 2.3) * mm});
            skLineSegment(sketch, "E636", {"start": v(24.54, 2.3) * mm, "end": v(24.54, 2.15) * mm});
            skLineSegment(sketch, "E637", {"start": v(24.54, 2.15) * mm, "end": v(24.43, 2.15) * mm});
            skLineSegment(sketch, "E638", {"start": v(24.43, 2.15) * mm, "end": v(24.33, 2.15) * mm});
            skLineSegment(sketch, "E639", {"start": v(24.33, 2.15) * mm, "end": v(24.33, 2.34) * mm});
            skLineSegment(sketch, "E640", {"start": v(24.33, 2.34) * mm, "end": v(24.33, 2.55) * mm});
            skLineSegment(sketch, "E641", {"start": v(24.33, 2.55) * mm, "end": v(24.2, 3.16) * mm});
            skLineSegment(sketch, "E642", {"start": v(24.2, 3.16) * mm, "end": v(23.9, 3.7) * mm});
            skLineSegment(sketch, "E643", {"start": v(23.9, 3.7) * mm, "end": v(23.83, 3.79) * mm});
            skLineSegment(sketch, "E644", {"start": v(23.83, 3.79) * mm, "end": v(23.74, 3.88) * mm});
            skLineSegment(sketch, "E645", {"start": v(23.74, 3.88) * mm, "end": v(23.22, 4.19) * mm});
            skLineSegment(sketch, "E646", {"start": v(23.22, 4.19) * mm, "end": v(22.57, 4.33) * mm});
            skLineSegment(sketch, "E647", {"start": v(22.57, 4.33) * mm, "end": v(22.42, 4.33) * mm});
            skLineSegment(sketch, "E648", {"start": v(22.42, 4.33) * mm, "end": v(21.95, 4.33) * mm});
            skLineSegment(sketch, "E649", {"start": v(21.95, 4.33) * mm, "end": v(20.9, 4.33) * mm});
            skLineSegment(sketch, "E650", {"start": v(20.9, 4.33) * mm, "end": v(19.87, 4.33) * mm});
            skLineSegment(sketch, "E651", {"start": v(19.87, 4.33) * mm, "end": v(19.4, 4.33) * mm});
            skLineSegment(sketch, "E652", {"start": v(19.4, 4.33) * mm, "end": v(19.4, 3.54) * mm});
            skLineSegment(sketch, "E653", {"start": v(19.4, 3.54) * mm, "end": v(19.4, 1.78) * mm});
            skLineSegment(sketch, "E654", {"start": v(19.4, 1.78) * mm, "end": v(19.4, 0.03) * mm});
            skLineSegment(sketch, "E655", {"start": v(19.4, 0.03) * mm, "end": v(19.4, -0.77) * mm});
            skLineSegment(sketch, "E656", {"start": v(19.4, -0.77) * mm, "end": v(19.77, -0.77) * mm});
            skLineSegment(sketch, "E657", {"start": v(19.77, -0.77) * mm, "end": v(20.6, -0.77) * mm});
            skLineSegment(sketch, "E658", {"start": v(20.6, -0.77) * mm, "end": v(21.42, -0.77) * mm});
            skLineSegment(sketch, "E659", {"start": v(21.42, -0.77) * mm, "end": v(21.8, -0.77) * mm});
            skLineSegment(sketch, "E660", {"start": v(21.8, -0.77) * mm, "end": v(21.9, -0.76) * mm});
            skLineSegment(sketch, "E661", {"start": v(21.9, -0.76) * mm, "end": v(22.43, -0.63) * mm});
            skLineSegment(sketch, "E662", {"start": v(22.43, -0.63) * mm, "end": v(22.87, -0.36) * mm});
            skLineSegment(sketch, "E663", {"start": v(22.87, -0.36) * mm, "end": v(22.94, -0.28) * mm});
            skLineSegment(sketch, "E664", {"start": v(22.94, -0.28) * mm, "end": v(23.02, -0.2) * mm});
            skLineSegment(sketch, "E665", {"start": v(23.02, -0.2) * mm, "end": v(23.27, 0.24) * mm});
            skLineSegment(sketch, "E666", {"start": v(23.27, 0.24) * mm, "end": v(23.39, 0.73) * mm});
            skLineSegment(sketch, "E667", {"start": v(23.39, 0.73) * mm, "end": v(23.39, 0.9) * mm});
            skLineSegment(sketch, "E668", {"start": v(23.39, 0.9) * mm, "end": v(23.39, 1.04) * mm});
            skLineSegment(sketch, "E669", {"start": v(23.39, 1.04) * mm, "end": v(23.5, 1.04) * mm});
            skLineSegment(sketch, "E670", {"start": v(23.5, 1.04) * mm, "end": v(23.6, 1.04) * mm});
            skLineSegment(sketch, "E671", {"start": v(23.6, 1.04) * mm, "end": v(23.6, 0.85) * mm});
            skLineSegment(sketch, "E672", {"start": v(23.6, 0.85) * mm, "end": v(23.6, 0.34) * mm});
            skLineSegment(sketch, "E673", {"start": v(23.6, 0.34) * mm, "end": v(23.6, -0.37) * mm});
            skLineSegment(sketch, "E674", {"start": v(23.6, -0.37) * mm, "end": v(23.6, -1.19) * mm});
            skLineSegment(sketch, "E675", {"start": v(23.6, -1.19) * mm, "end": v(23.6, -2) * mm});
            skLineSegment(sketch, "E676", {"start": v(23.6, -2) * mm, "end": v(23.6, -2.71) * mm});
            skLineSegment(sketch, "E677", {"start": v(23.6, -2.71) * mm, "end": v(23.6, -3.22) * mm});
            skLineSegment(sketch, "E678", {"start": v(23.6, -3.22) * mm, "end": v(23.6, -3.4) * mm});
            skLineSegment(sketch, "E679", {"start": v(23.6, -3.4) * mm, "end": v(23.5, -3.4) * mm});
            skLineSegment(sketch, "E680", {"start": v(23.5, -3.4) * mm, "end": v(23.39, -3.4) * mm});
            skLineSegment(sketch, "E681", {"start": v(23.39, -3.4) * mm, "end": v(23.39, -3.26) * mm});
            skLineSegment(sketch, "E682", {"start": v(23.39, -3.26) * mm, "end": v(23.39, -3.05) * mm});
            skLineSegment(sketch, "E683", {"start": v(23.39, -3.05) * mm, "end": v(23.2, -2.41) * mm});
            skLineSegment(sketch, "E684", {"start": v(23.2, -2.41) * mm, "end": v(22.77, -1.9) * mm});
            skLineSegment(sketch, "E685", {"start": v(22.77, -1.9) * mm, "end": v(22.65, -1.84) * mm});
            skLineSegment(sketch, "E686", {"start": v(22.65, -1.84) * mm, "end": v(22.59, -1.8) * mm});
            skLineSegment(sketch, "E687", {"start": v(22.59, -1.8) * mm, "end": v(22, -1.6) * mm});
            skLineSegment(sketch, "E688", {"start": v(22, -1.6) * mm, "end": v(21.81, -1.6) * mm});
            skLineSegment(sketch, "E689", {"start": v(21.81, -1.6) * mm, "end": v(21.43, -1.6) * mm});
            skLineSegment(sketch, "E690", {"start": v(21.43, -1.6) * mm, "end": v(20.6, -1.6) * mm});
            skLineSegment(sketch, "E691", {"start": v(20.6, -1.6) * mm, "end": v(19.77, -1.6) * mm});
            skLineSegment(sketch, "E692", {"start": v(19.77, -1.6) * mm, "end": v(19.4, -1.6) * mm});
            skLineSegment(sketch, "E693", {"start": v(19.4, -1.6) * mm, "end": v(19.4, -2.38) * mm});
            skLineSegment(sketch, "E694", {"start": v(19.4, -2.38) * mm, "end": v(19.4, -4.1) * mm});
            skLineSegment(sketch, "E695", {"start": v(19.4, -4.1) * mm, "end": v(19.4, -5.8) * mm});
            skLineSegment(sketch, "E696", {"start": v(19.4, -5.8) * mm, "end": v(19.4, -6.58) * mm});
            skLineSegment(sketch, "E697", {"start": v(19.4, -6.58) * mm, "end": v(19.8, -6.58) * mm});
            skLineSegment(sketch, "E698", {"start": v(19.8, -6.58) * mm, "end": v(20.66, -6.58) * mm});
            skLineSegment(sketch, "E699", {"start": v(20.66, -6.58) * mm, "end": v(21.52, -6.58) * mm});
            skLineSegment(sketch, "E700", {"start": v(21.52, -6.58) * mm, "end": v(21.92, -6.58) * mm});
            skLineSegment(sketch, "E701", {"start": v(21.92, -6.58) * mm, "end": v(22.13, -6.57) * mm});
            skLineSegment(sketch, "E702", {"start": v(22.13, -6.57) * mm, "end": v(23.12, -6.36) * mm});
            skLineSegment(sketch, "E703", {"start": v(23.12, -6.36) * mm, "end": v(23.98, -5.9) * mm});
            skLineSegment(sketch, "E704", {"start": v(23.98, -5.9) * mm, "end": v(24.13, -5.77) * mm});
            skLineSegment(sketch, "E705", {"start": v(24.13, -5.77) * mm, "end": v(24.28, -5.64) * mm});
            skLineSegment(sketch, "E706", {"start": v(24.28, -5.64) * mm, "end": v(24.92, -4.82) * mm});
            skLineSegment(sketch, "E707", {"start": v(24.92, -4.82) * mm, "end": v(25.4, -3.8) * mm});
            skLineSegment(sketch, "E708", {"start": v(25.4, -3.8) * mm, "end": v(25.46, -3.56) * mm});
            skLineSegment(sketch, "E709", {"start": v(25.46, -3.56) * mm, "end": v(25.65, -3.56) * mm});
            skLineSegment(sketch, "E710", {"start": v(25.65, -3.56) * mm, "end": v(25.62, -3.72) * mm});
            skLineSegment(sketch, "E711", {"start": v(25.62, -3.72) * mm, "end": v(25.53, -4.16) * mm});
            skLineSegment(sketch, "E712", {"start": v(25.53, -4.16) * mm, "end": v(25.4, -4.78) * mm});
            skLineSegment(sketch, "E713", {"start": v(25.4, -4.78) * mm, "end": v(25.25, -5.49) * mm});
            skLineSegment(sketch, "E714", {"start": v(25.25, -5.49) * mm, "end": v(25.1, -6.2) * mm});
            skLineSegment(sketch, "E715", {"start": v(25.1, -6.2) * mm, "end": v(24.98, -6.81) * mm});
            skLineSegment(sketch, "E716", {"start": v(24.98, -6.81) * mm, "end": v(24.89, -7.25) * mm});
            skLineSegment(sketch, "E717", {"start": v(24.89, -7.25) * mm, "end": v(24.85, -7.42) * mm});
            skLineSegment(sketch, "E718", {"start": v(26.7, -7.42) * mm, "end": v(26.7, -7.31) * mm});
            skLineSegment(sketch, "E719", {"start": v(26.7, -7.31) * mm, "end": v(26.7, -7.2) * mm});
            skLineSegment(sketch, "E720", {"start": v(26.7, -7.2) * mm, "end": v(26.83, -7.2) * mm});
            skLineSegment(sketch, "E721", {"start": v(26.83, -7.2) * mm, "end": v(26.95, -7.2) * mm});
            skLineSegment(sketch, "E722", {"start": v(26.95, -7.2) * mm, "end": v(27.15, -7.2) * mm});
            skLineSegment(sketch, "E723", {"start": v(27.15, -7.2) * mm, "end": v(27.7, -6.94) * mm});
            skLineSegment(sketch, "E724", {"start": v(27.7, -6.94) * mm, "end": v(27.76, -6.9) * mm});
            skLineSegment(sketch, "E725", {"start": v(27.76, -6.9) * mm, "end": v(27.81, -6.84) * mm});
            skLineSegment(sketch, "E726", {"start": v(27.81, -6.84) * mm, "end": v(28.09, -6.3) * mm});
            skLineSegment(sketch, "E727", {"start": v(28.09, -6.3) * mm, "end": v(28.09, -6.12) * mm});
            skLineSegment(sketch, "E728", {"start": v(28.09, -6.12) * mm, "end": v(28.09, -5.69) * mm});
            skLineSegment(sketch, "E729", {"start": v(28.09, -5.69) * mm, "end": v(28.09, -4.56) * mm});
            skLineSegment(sketch, "E730", {"start": v(28.09, -4.56) * mm, "end": v(28.09, -2.96) * mm});
            skLineSegment(sketch, "E731", {"start": v(28.09, -2.96) * mm, "end": v(28.09, -1.13) * mm});
            skLineSegment(sketch, "E732", {"start": v(28.09, -1.13) * mm, "end": v(28.09, 0.7) * mm});
            skLineSegment(sketch, "E733", {"start": v(28.09, 0.7) * mm, "end": v(28.09, 2.3) * mm});
            skLineSegment(sketch, "E734", {"start": v(28.09, 2.3) * mm, "end": v(28.09, 3.42) * mm});
            skLineSegment(sketch, "E735", {"start": v(28.09, 3.42) * mm, "end": v(28.09, 3.85) * mm});
            skLineSegment(sketch, "E736", {"start": v(28.09, 3.85) * mm, "end": v(28.09, 4.05) * mm});
            skLineSegment(sketch, "E737", {"start": v(28.09, 4.05) * mm, "end": v(27.8, 4.58) * mm});
            skLineSegment(sketch, "E738", {"start": v(27.8, 4.58) * mm, "end": v(27.75, 4.64) * mm});
            skLineSegment(sketch, "E739", {"start": v(27.75, 4.64) * mm, "end": v(27.7, 4.7) * mm});
            skLineSegment(sketch, "E740", {"start": v(27.7, 4.7) * mm, "end": v(27.14, 4.96) * mm});
            skLineSegment(sketch, "E741", {"start": v(27.14, 4.96) * mm, "end": v(26.95, 4.96) * mm});
            skLineSegment(sketch, "E742", {"start": v(26.95, 4.96) * mm, "end": v(26.83, 4.96) * mm});
            skLineSegment(sketch, "E743", {"start": v(26.83, 4.96) * mm, "end": v(26.7, 4.96) * mm});
            skLineSegment(sketch, "E744", {"start": v(26.7, 4.96) * mm, "end": v(26.7, 5.07) * mm});
            skLineSegment(sketch, "E745", {"start": v(26.7, 5.07) * mm, "end": v(26.7, 5.17) * mm});
            skLineSegment(sketch, "E746", {"start": v(26.7, 5.17) * mm, "end": v(27.61, 5.17) * mm});
            skLineSegment(sketch, "E747", {"start": v(27.61, 5.17) * mm, "end": v(29.62, 5.17) * mm});
            skLineSegment(sketch, "E748", {"start": v(29.62, 5.17) * mm, "end": v(31.62, 5.17) * mm});
            skLineSegment(sketch, "E749", {"start": v(31.62, 5.17) * mm, "end": v(32.53, 5.17) * mm});
            skLineSegment(sketch, "E750", {"start": v(32.53, 5.17) * mm, "end": v(32.53, 5.07) * mm});
            skLineSegment(sketch, "E751", {"start": v(32.53, 5.07) * mm, "end": v(32.53, 4.96) * mm});
            skLineSegment(sketch, "E752", {"start": v(32.53, 4.96) * mm, "end": v(32.4, 4.96) * mm});
            skLineSegment(sketch, "E753", {"start": v(32.4, 4.96) * mm, "end": v(32.28, 4.96) * mm});
            skLineSegment(sketch, "E754", {"start": v(32.28, 4.96) * mm, "end": v(32.08, 4.96) * mm});
            skLineSegment(sketch, "E755", {"start": v(32.08, 4.96) * mm, "end": v(31.52, 4.7) * mm});
            skLineSegment(sketch, "E756", {"start": v(31.52, 4.7) * mm, "end": v(31.46, 4.65) * mm});
            skLineSegment(sketch, "E757", {"start": v(31.46, 4.65) * mm, "end": v(31.4, 4.6) * mm});
            skLineSegment(sketch, "E758", {"start": v(31.4, 4.6) * mm, "end": v(31.13, 4.04) * mm});
            skLineSegment(sketch, "E759", {"start": v(31.13, 4.04) * mm, "end": v(31.13, 3.85) * mm});
            skLineSegment(sketch, "E760", {"start": v(31.13, 3.85) * mm, "end": v(31.13, 3.4) * mm});
            skLineSegment(sketch, "E761", {"start": v(31.13, 3.4) * mm, "end": v(31.13, 2.22) * mm});
            skLineSegment(sketch, "E762", {"start": v(31.13, 2.22) * mm, "end": v(31.13, 0.55) * mm});
            skLineSegment(sketch, "E763", {"start": v(31.13, 0.55) * mm, "end": v(31.13, -1.36) * mm});
            skLineSegment(sketch, "E764", {"start": v(31.13, -1.36) * mm, "end": v(31.13, -3.28) * mm});
            skLineSegment(sketch, "E765", {"start": v(31.13, -3.28) * mm, "end": v(31.13, -4.95) * mm});
            skLineSegment(sketch, "E766", {"start": v(31.13, -4.95) * mm, "end": v(31.13, -6.13) * mm});
            skLineSegment(sketch, "E767", {"start": v(31.13, -6.13) * mm, "end": v(31.13, -6.58) * mm});
            skLineSegment(sketch, "E768", {"start": v(31.13, -6.58) * mm, "end": v(31.52, -6.58) * mm});
            skLineSegment(sketch, "E769", {"start": v(31.52, -6.58) * mm, "end": v(32.39, -6.58) * mm});
            skLineSegment(sketch, "E770", {"start": v(32.39, -6.58) * mm, "end": v(33.25, -6.58) * mm});
            skLineSegment(sketch, "E771", {"start": v(33.25, -6.58) * mm, "end": v(33.65, -6.58) * mm});
            skLineSegment(sketch, "E772", {"start": v(33.65, -6.58) * mm, "end": v(33.86, -6.57) * mm});
            skLineSegment(sketch, "E773", {"start": v(33.86, -6.57) * mm, "end": v(34.85, -6.36) * mm});
            skLineSegment(sketch, "E774", {"start": v(34.85, -6.36) * mm, "end": v(35.7, -5.9) * mm});
            skLineSegment(sketch, "E775", {"start": v(35.7, -5.9) * mm, "end": v(35.85, -5.77) * mm});
            skLineSegment(sketch, "E776", {"start": v(35.85, -5.77) * mm, "end": v(36, -5.64) * mm});
            skLineSegment(sketch, "E777", {"start": v(36, -5.64) * mm, "end": v(36.63, -4.82) * mm});
            skLineSegment(sketch, "E778", {"start": v(36.63, -4.82) * mm, "end": v(37.1, -3.8) * mm});
            skLineSegment(sketch, "E779", {"start": v(37.1, -3.8) * mm, "end": v(37.17, -3.56) * mm});
            skLineSegment(sketch, "E780", {"start": v(37.17, -3.56) * mm, "end": v(37.29, -3.56) * mm});
            skLineSegment(sketch, "E781", {"start": v(37.29, -3.56) * mm, "end": v(37.4, -3.56) * mm});
            skLineSegment(sketch, "E782", {"start": v(37.4, -3.56) * mm, "end": v(37.37, -3.72) * mm});
            skLineSegment(sketch, "E783", {"start": v(37.37, -3.72) * mm, "end": v(37.27, -4.16) * mm});
            skLineSegment(sketch, "E784", {"start": v(37.27, -4.16) * mm, "end": v(37.14, -4.78) * mm});
            skLineSegment(sketch, "E785", {"start": v(37.14, -4.78) * mm, "end": v(37, -5.49) * mm});
            skLineSegment(sketch, "E786", {"start": v(37, -5.49) * mm, "end": v(36.84, -6.2) * mm});
            skLineSegment(sketch, "E787", {"start": v(36.84, -6.2) * mm, "end": v(36.71, -6.81) * mm});
            skLineSegment(sketch, "E788", {"start": v(36.71, -6.81) * mm, "end": v(36.62, -7.25) * mm});
            skLineSegment(sketch, "E789", {"start": v(36.62, -7.25) * mm, "end": v(36.58, -7.42) * mm});
            skLineSegment(sketch, "E790", {"start": v(36.58, -7.42) * mm, "end": v(36.16, -7.42) * mm});
            skLineSegment(sketch, "E791", {"start": v(36.16, -7.42) * mm, "end": v(35.04, -7.42) * mm});
            skLineSegment(sketch, "E792", {"start": v(35.04, -7.42) * mm, "end": v(33.46, -7.42) * mm});
            skLineSegment(sketch, "E793", {"start": v(33.46, -7.42) * mm, "end": v(31.64, -7.42) * mm});
            skLineSegment(sketch, "E794", {"start": v(31.64, -7.42) * mm, "end": v(29.83, -7.42) * mm});
            skLineSegment(sketch, "E795", {"start": v(29.83, -7.42) * mm, "end": v(28.24, -7.42) * mm});
            skLineSegment(sketch, "E796", {"start": v(28.24, -7.42) * mm, "end": v(27.12, -7.42) * mm});
            skLineSegment(sketch, "E797", {"start": v(27.12, -7.42) * mm, "end": v(26.7, -7.42) * mm});
            skLineSegment(sketch, "E798", {"start": v(38.01, -7.42) * mm, "end": v(38.01, -7.31) * mm});
            skLineSegment(sketch, "E799", {"start": v(38.01, -7.31) * mm, "end": v(38.01, -7.2) * mm});
            skLineSegment(sketch, "E800", {"start": v(38.01, -7.2) * mm, "end": v(38.14, -7.2) * mm});
            skLineSegment(sketch, "E801", {"start": v(38.14, -7.2) * mm, "end": v(38.26, -7.2) * mm});
            skLineSegment(sketch, "E802", {"start": v(38.26, -7.2) * mm, "end": v(38.46, -7.2) * mm});
            skLineSegment(sketch, "E803", {"start": v(38.46, -7.2) * mm, "end": v(39.02, -6.94) * mm});
            skLineSegment(sketch, "E804", {"start": v(39.02, -6.94) * mm, "end": v(39.07, -6.9) * mm});
            skLineSegment(sketch, "E805", {"start": v(39.07, -6.9) * mm, "end": v(39.12, -6.84) * mm});
            skLineSegment(sketch, "E806", {"start": v(39.12, -6.84) * mm, "end": v(39.4, -6.3) * mm});
            skLineSegment(sketch, "E807", {"start": v(39.4, -6.3) * mm, "end": v(39.4, -6.12) * mm});
            skLineSegment(sketch, "E808", {"start": v(39.4, -6.12) * mm, "end": v(39.4, -5.69) * mm});
            skLineSegment(sketch, "E809", {"start": v(39.4, -5.69) * mm, "end": v(39.4, -4.56) * mm});
            skLineSegment(sketch, "E810", {"start": v(39.4, -4.56) * mm, "end": v(39.4, -2.96) * mm});
            skLineSegment(sketch, "E811", {"start": v(39.4, -2.96) * mm, "end": v(39.4, -1.13) * mm});
            skLineSegment(sketch, "E812", {"start": v(39.4, -1.13) * mm, "end": v(39.4, 0.7) * mm});
            skLineSegment(sketch, "E813", {"start": v(39.4, 0.7) * mm, "end": v(39.4, 2.3) * mm});
            skLineSegment(sketch, "E814", {"start": v(39.4, 2.3) * mm, "end": v(39.4, 3.42) * mm});
            skLineSegment(sketch, "E815", {"start": v(39.4, 3.42) * mm, "end": v(39.4, 3.85) * mm});
            skLineSegment(sketch, "E816", {"start": v(39.4, 3.85) * mm, "end": v(39.4, 4.05) * mm});
            skLineSegment(sketch, "E817", {"start": v(39.4, 4.05) * mm, "end": v(39.11, 4.58) * mm});
            skLineSegment(sketch, "E818", {"start": v(39.11, 4.58) * mm, "end": v(39.06, 4.64) * mm});
            skLineSegment(sketch, "E819", {"start": v(39.06, 4.64) * mm, "end": v(39, 4.7) * mm});
            skLineSegment(sketch, "E820", {"start": v(39, 4.7) * mm, "end": v(38.45, 4.96) * mm});
            skLineSegment(sketch, "E821", {"start": v(38.45, 4.96) * mm, "end": v(38.26, 4.96) * mm});
            skLineSegment(sketch, "E822", {"start": v(38.26, 4.96) * mm, "end": v(38.14, 4.96) * mm});
            skLineSegment(sketch, "E823", {"start": v(38.14, 4.96) * mm, "end": v(38.01, 4.96) * mm});
            skLineSegment(sketch, "E824", {"start": v(38.01, 4.96) * mm, "end": v(38.01, 5.07) * mm});
            skLineSegment(sketch, "E825", {"start": v(38.01, 5.07) * mm, "end": v(38.01, 5.17) * mm});
            skLineSegment(sketch, "E826", {"start": v(38.01, 5.17) * mm, "end": v(38.92, 5.17) * mm});
            skLineSegment(sketch, "E827", {"start": v(38.92, 5.17) * mm, "end": v(40.93, 5.17) * mm});
            skLineSegment(sketch, "E828", {"start": v(40.93, 5.17) * mm, "end": v(42.93, 5.17) * mm});
            skLineSegment(sketch, "E829", {"start": v(42.93, 5.17) * mm, "end": v(43.84, 5.17) * mm});
            skLineSegment(sketch, "E830", {"start": v(43.84, 5.17) * mm, "end": v(43.84, 5.07) * mm});
            skLineSegment(sketch, "E831", {"start": v(43.84, 5.07) * mm, "end": v(43.84, 4.96) * mm});
            skLineSegment(sketch, "E832", {"start": v(43.84, 4.96) * mm, "end": v(43.72, 4.96) * mm});
            skLineSegment(sketch, "E833", {"start": v(43.72, 4.96) * mm, "end": v(43.6, 4.96) * mm});
            skLineSegment(sketch, "E834", {"start": v(43.6, 4.96) * mm, "end": v(43.39, 4.96) * mm});
            skLineSegment(sketch, "E835", {"start": v(43.39, 4.96) * mm, "end": v(42.83, 4.7) * mm});
            skLineSegment(sketch, "E836", {"start": v(42.83, 4.7) * mm, "end": v(42.77, 4.65) * mm});
            skLineSegment(sketch, "E837", {"start": v(42.77, 4.65) * mm, "end": v(42.72, 4.6) * mm});
            skLineSegment(sketch, "E838", {"start": v(42.72, 4.6) * mm, "end": v(42.44, 4.04) * mm});
            skLineSegment(sketch, "E839", {"start": v(42.44, 4.04) * mm, "end": v(42.44, 3.85) * mm});
            skLineSegment(sketch, "E840", {"start": v(42.44, 3.85) * mm, "end": v(42.44, 3.4) * mm});
            skLineSegment(sketch, "E841", {"start": v(42.44, 3.4) * mm, "end": v(42.44, 2.22) * mm});
            skLineSegment(sketch, "E842", {"start": v(42.44, 2.22) * mm, "end": v(42.44, 0.55) * mm});
            skLineSegment(sketch, "E843", {"start": v(42.44, 0.55) * mm, "end": v(42.44, -1.36) * mm});
            skLineSegment(sketch, "E844", {"start": v(42.44, -1.36) * mm, "end": v(42.44, -3.28) * mm});
            skLineSegment(sketch, "E845", {"start": v(42.44, -3.28) * mm, "end": v(42.44, -4.95) * mm});
            skLineSegment(sketch, "E846", {"start": v(42.44, -4.95) * mm, "end": v(42.44, -6.13) * mm});
            skLineSegment(sketch, "E847", {"start": v(42.44, -6.13) * mm, "end": v(42.44, -6.58) * mm});
            skLineSegment(sketch, "E848", {"start": v(42.44, -6.58) * mm, "end": v(42.83, -6.58) * mm});
            skLineSegment(sketch, "E849", {"start": v(42.83, -6.58) * mm, "end": v(43.7, -6.58) * mm});
            skLineSegment(sketch, "E850", {"start": v(43.7, -6.58) * mm, "end": v(44.56, -6.58) * mm});
            skLineSegment(sketch, "E851", {"start": v(44.56, -6.58) * mm, "end": v(44.96, -6.58) * mm});
            skLineSegment(sketch, "E852", {"start": v(44.96, -6.58) * mm, "end": v(45.17, -6.57) * mm});
            skLineSegment(sketch, "E853", {"start": v(45.17, -6.57) * mm, "end": v(46.16, -6.36) * mm});
            skLineSegment(sketch, "E854", {"start": v(46.16, -6.36) * mm, "end": v(47, -5.9) * mm});
            skLineSegment(sketch, "E855", {"start": v(47, -5.9) * mm, "end": v(47.16, -5.77) * mm});
            skLineSegment(sketch, "E856", {"start": v(47.16, -5.77) * mm, "end": v(47.3, -5.64) * mm});
            skLineSegment(sketch, "E857", {"start": v(47.3, -5.64) * mm, "end": v(47.94, -4.82) * mm});
            skLineSegment(sketch, "E858", {"start": v(47.94, -4.82) * mm, "end": v(48.41, -3.8) * mm});
            skLineSegment(sketch, "E859", {"start": v(48.41, -3.8) * mm, "end": v(48.48, -3.56) * mm});
            skLineSegment(sketch, "E860", {"start": v(48.48, -3.56) * mm, "end": v(48.6, -3.56) * mm});
            skLineSegment(sketch, "E861", {"start": v(48.6, -3.56) * mm, "end": v(48.71, -3.56) * mm});
            skLineSegment(sketch, "E862", {"start": v(48.71, -3.56) * mm, "end": v(48.68, -3.72) * mm});
            skLineSegment(sketch, "E863", {"start": v(48.68, -3.72) * mm, "end": v(48.58, -4.16) * mm});
            skLineSegment(sketch, "E864", {"start": v(48.58, -4.16) * mm, "end": v(48.45, -4.78) * mm});
            skLineSegment(sketch, "E865", {"start": v(48.45, -4.78) * mm, "end": v(48.3, -5.49) * mm});
            skLineSegment(sketch, "E866", {"start": v(48.3, -5.49) * mm, "end": v(48.15, -6.2) * mm});
            skLineSegment(sketch, "E867", {"start": v(48.15, -6.2) * mm, "end": v(48.02, -6.81) * mm});
            skLineSegment(sketch, "E868", {"start": v(48.02, -6.81) * mm, "end": v(47.93, -7.25) * mm});
            skLineSegment(sketch, "E869", {"start": v(47.93, -7.25) * mm, "end": v(47.9, -7.42) * mm});
            skLineSegment(sketch, "E870", {"start": v(47.9, -7.42) * mm, "end": v(47.47, -7.42) * mm});
            skLineSegment(sketch, "E871", {"start": v(47.47, -7.42) * mm, "end": v(46.35, -7.42) * mm});
            skLineSegment(sketch, "E872", {"start": v(46.35, -7.42) * mm, "end": v(44.77, -7.42) * mm});
            skLineSegment(sketch, "E873", {"start": v(44.77, -7.42) * mm, "end": v(42.95, -7.42) * mm});
            skLineSegment(sketch, "E874", {"start": v(42.95, -7.42) * mm, "end": v(41.14, -7.42) * mm});
            skLineSegment(sketch, "E875", {"start": v(41.14, -7.42) * mm, "end": v(39.55, -7.42) * mm});
            skLineSegment(sketch, "E876", {"start": v(39.55, -7.42) * mm, "end": v(38.44, -7.42) * mm});
            skLineSegment(sketch, "E877", {"start": v(38.44, -7.42) * mm, "end": v(38.01, -7.42) * mm});
            skLineSegment(sketch, "E878", {"start": v(59.2, -7.42) * mm, "end": v(58.78, -7.42) * mm});
            skLineSegment(sketch, "E879", {"start": v(58.78, -7.42) * mm, "end": v(57.66, -7.42) * mm});
            skLineSegment(sketch, "E880", {"start": v(57.66, -7.42) * mm, "end": v(56.08, -7.42) * mm});
            skLineSegment(sketch, "E881", {"start": v(56.08, -7.42) * mm, "end": v(54.26, -7.42) * mm});
            skLineSegment(sketch, "E882", {"start": v(54.26, -7.42) * mm, "end": v(52.45, -7.42) * mm});
            skLineSegment(sketch, "E883", {"start": v(52.45, -7.42) * mm, "end": v(50.86, -7.42) * mm});
            skLineSegment(sketch, "E884", {"start": v(50.86, -7.42) * mm, "end": v(49.74, -7.42) * mm});
            skLineSegment(sketch, "E885", {"start": v(49.74, -7.42) * mm, "end": v(49.32, -7.42) * mm});
            skLineSegment(sketch, "E886", {"start": v(49.32, -7.42) * mm, "end": v(49.32, -7.31) * mm});
            skLineSegment(sketch, "E887", {"start": v(49.32, -7.31) * mm, "end": v(49.32, -7.2) * mm});
            skLineSegment(sketch, "E888", {"start": v(49.32, -7.2) * mm, "end": v(49.45, -7.2) * mm});
            skLineSegment(sketch, "E889", {"start": v(49.45, -7.2) * mm, "end": v(49.57, -7.2) * mm});
            skLineSegment(sketch, "E890", {"start": v(49.57, -7.2) * mm, "end": v(49.77, -7.2) * mm});
            skLineSegment(sketch, "E891", {"start": v(49.77, -7.2) * mm, "end": v(50.33, -6.94) * mm});
            skLineSegment(sketch, "E892", {"start": v(50.33, -6.94) * mm, "end": v(50.38, -6.9) * mm});
            skLineSegment(sketch, "E893", {"start": v(50.38, -6.9) * mm, "end": v(50.43, -6.84) * mm});
            skLineSegment(sketch, "E894", {"start": v(50.43, -6.84) * mm, "end": v(50.72, -6.2) * mm});
            skLineSegment(sketch, "E895", {"start": v(50.72, -6.2) * mm, "end": v(50.73, -6.12) * mm});
            skLineSegment(sketch, "E896", {"start": v(50.73, -6.12) * mm, "end": v(50.73, -5.69) * mm});
            skLineSegment(sketch, "E897", {"start": v(50.73, -5.69) * mm, "end": v(50.73, -4.56) * mm});
            skLineSegment(sketch, "E898", {"start": v(50.73, -4.56) * mm, "end": v(50.73, -2.95) * mm});
            skLineSegment(sketch, "E899", {"start": v(50.73, -2.95) * mm, "end": v(50.73, -1.12) * mm});
            skLineSegment(sketch, "E900", {"start": v(50.73, -1.12) * mm, "end": v(50.73, 0.71) * mm});
            skLineSegment(sketch, "E901", {"start": v(50.73, 0.71) * mm, "end": v(50.73, 2.31) * mm});
            skLineSegment(sketch, "E902", {"start": v(50.73, 2.31) * mm, "end": v(50.73, 3.44) * mm});
            skLineSegment(sketch, "E903", {"start": v(50.73, 3.44) * mm, "end": v(50.73, 3.87) * mm});
            skLineSegment(sketch, "E904", {"start": v(50.73, 3.87) * mm, "end": v(50.72, 3.95) * mm});
            skLineSegment(sketch, "E905", {"start": v(50.72, 3.95) * mm, "end": v(50.43, 4.6) * mm});
            skLineSegment(sketch, "E906", {"start": v(50.43, 4.6) * mm, "end": v(50.38, 4.65) * mm});
            skLineSegment(sketch, "E907", {"start": v(50.38, 4.65) * mm, "end": v(50.33, 4.7) * mm});
            skLineSegment(sketch, "E908", {"start": v(50.33, 4.7) * mm, "end": v(49.76, 4.96) * mm});
            skLineSegment(sketch, "E909", {"start": v(49.76, 4.96) * mm, "end": v(49.57, 4.96) * mm});
            skLineSegment(sketch, "E910", {"start": v(49.57, 4.96) * mm, "end": v(49.45, 4.96) * mm});
            skLineSegment(sketch, "E911", {"start": v(49.45, 4.96) * mm, "end": v(49.32, 4.96) * mm});
            skLineSegment(sketch, "E912", {"start": v(49.32, 4.96) * mm, "end": v(49.32, 5.07) * mm});
            skLineSegment(sketch, "E913", {"start": v(49.32, 5.07) * mm, "end": v(49.32, 5.17) * mm});
            skLineSegment(sketch, "E914", {"start": v(49.32, 5.17) * mm, "end": v(49.64, 5.17) * mm});
            skLineSegment(sketch, "E915", {"start": v(49.64, 5.17) * mm, "end": v(50.47, 5.17) * mm});
            skLineSegment(sketch, "E916", {"start": v(50.47, 5.17) * mm, "end": v(51.66, 5.17) * mm});
            skLineSegment(sketch, "E917", {"start": v(51.66, 5.17) * mm, "end": v(53.01, 5.17) * mm});
            skLineSegment(sketch, "E918", {"start": v(53.01, 5.17) * mm, "end": v(54.37, 5.17) * mm});
            skLineSegment(sketch, "E919", {"start": v(54.37, 5.17) * mm, "end": v(55.55, 5.17) * mm});
            skLineSegment(sketch, "E920", {"start": v(55.55, 5.17) * mm, "end": v(56.39, 5.17) * mm});
            skLineSegment(sketch, "E921", {"start": v(56.39, 5.17) * mm, "end": v(56.7, 5.17) * mm});
            skLineSegment(sketch, "E922", {"start": v(56.7, 5.17) * mm, "end": v(57.02, 5.17) * mm});
            skLineSegment(sketch, "E923", {"start": v(57.02, 5.17) * mm, "end": v(57.83, 5.26) * mm});
            skLineSegment(sketch, "E924", {"start": v(57.83, 5.26) * mm, "end": v(57.94, 5.28) * mm});
            skLineSegment(sketch, "E925", {"start": v(57.94, 5.28) * mm, "end": v(58.06, 5.3) * mm});
            skLineSegment(sketch, "E926", {"start": v(58.06, 5.3) * mm, "end": v(58.84, 5.47) * mm});
            skLineSegment(sketch, "E927", {"start": v(58.84, 5.47) * mm, "end": v(58.89, 5.49) * mm});
            skLineSegment(sketch, "E928", {"start": v(58.89, 5.49) * mm, "end": v(58.89, 5.34) * mm});
            skLineSegment(sketch, "E929", {"start": v(58.89, 5.34) * mm, "end": v(58.89, 4.97) * mm});
            skLineSegment(sketch, "E930", {"start": v(58.89, 4.97) * mm, "end": v(58.89, 4.43) * mm});
            skLineSegment(sketch, "E931", {"start": v(58.89, 4.43) * mm, "end": v(58.89, 3.82) * mm});
            skLineSegment(sketch, "E932", {"start": v(58.89, 3.82) * mm, "end": v(58.89, 3.2) * mm});
            skLineSegment(sketch, "E933", {"start": v(58.89, 3.2) * mm, "end": v(58.89, 2.67) * mm});
            skLineSegment(sketch, "E934", {"start": v(58.89, 2.67) * mm, "end": v(58.89, 2.3) * mm});
            skLineSegment(sketch, "E935", {"start": v(58.89, 2.3) * mm, "end": v(58.89, 2.15) * mm});
            skLineSegment(sketch, "E936", {"start": v(58.89, 2.15) * mm, "end": v(58.78, 2.15) * mm});
            skLineSegment(sketch, "E937", {"start": v(58.78, 2.15) * mm, "end": v(58.68, 2.15) * mm});
            skLineSegment(sketch, "E938", {"start": v(58.68, 2.15) * mm, "end": v(58.68, 2.34) * mm});
            skLineSegment(sketch, "E939", {"start": v(58.68, 2.34) * mm, "end": v(58.68, 2.55) * mm});
            skLineSegment(sketch, "E940", {"start": v(58.68, 2.55) * mm, "end": v(58.55, 3.16) * mm});
            skLineSegment(sketch, "E941", {"start": v(58.55, 3.16) * mm, "end": v(58.26, 3.7) * mm});
            skLineSegment(sketch, "E942", {"start": v(58.26, 3.7) * mm, "end": v(58.17, 3.79) * mm});
            skLineSegment(sketch, "E943", {"start": v(58.17, 3.79) * mm, "end": v(58.1, 3.88) * mm});
            skLineSegment(sketch, "E944", {"start": v(58.1, 3.88) * mm, "end": v(57.57, 4.19) * mm});
            skLineSegment(sketch, "E945", {"start": v(57.57, 4.19) * mm, "end": v(56.92, 4.33) * mm});
            skLineSegment(sketch, "E946", {"start": v(56.92, 4.33) * mm, "end": v(56.77, 4.33) * mm});
            skLineSegment(sketch, "E947", {"start": v(56.77, 4.33) * mm, "end": v(56.3, 4.33) * mm});
            skLineSegment(sketch, "E948", {"start": v(56.3, 4.33) * mm, "end": v(55.26, 4.33) * mm});
            skLineSegment(sketch, "E949", {"start": v(55.26, 4.33) * mm, "end": v(54.22, 4.33) * mm});
            skLineSegment(sketch, "E950", {"start": v(54.22, 4.33) * mm, "end": v(53.75, 4.33) * mm});
            skLineSegment(sketch, "E951", {"start": v(53.75, 4.33) * mm, "end": v(53.75, 3.54) * mm});
            skLineSegment(sketch, "E952", {"start": v(53.75, 3.54) * mm, "end": v(53.75, 1.78) * mm});
            skLineSegment(sketch, "E953", {"start": v(53.75, 1.78) * mm, "end": v(53.75, 0.03) * mm});
            skLineSegment(sketch, "E954", {"start": v(53.75, 0.03) * mm, "end": v(53.75, -0.77) * mm});
            skLineSegment(sketch, "E955", {"start": v(53.75, -0.77) * mm, "end": v(54.12, -0.77) * mm});
            skLineSegment(sketch, "E956", {"start": v(54.12, -0.77) * mm, "end": v(54.94, -0.77) * mm});
            skLineSegment(sketch, "E957", {"start": v(54.94, -0.77) * mm, "end": v(55.76, -0.77) * mm});
            skLineSegment(sketch, "E958", {"start": v(55.76, -0.77) * mm, "end": v(56.14, -0.77) * mm});
            skLineSegment(sketch, "E959", {"start": v(56.14, -0.77) * mm, "end": v(56.26, -0.76) * mm});
            skLineSegment(sketch, "E960", {"start": v(56.26, -0.76) * mm, "end": v(56.78, -0.63) * mm});
            skLineSegment(sketch, "E961", {"start": v(56.78, -0.63) * mm, "end": v(57.22, -0.36) * mm});
            skLineSegment(sketch, "E962", {"start": v(57.22, -0.36) * mm, "end": v(57.3, -0.28) * mm});
            skLineSegment(sketch, "E963", {"start": v(57.3, -0.28) * mm, "end": v(57.37, -0.2) * mm});
            skLineSegment(sketch, "E964", {"start": v(57.37, -0.2) * mm, "end": v(57.62, 0.24) * mm});
            skLineSegment(sketch, "E965", {"start": v(57.62, 0.24) * mm, "end": v(57.73, 0.73) * mm});
            skLineSegment(sketch, "E966", {"start": v(57.73, 0.73) * mm, "end": v(57.73, 0.9) * mm});
            skLineSegment(sketch, "E967", {"start": v(57.73, 0.9) * mm, "end": v(57.73, 1.04) * mm});
            skLineSegment(sketch, "E968", {"start": v(57.73, 1.04) * mm, "end": v(57.84, 1.04) * mm});
            skLineSegment(sketch, "E969", {"start": v(57.84, 1.04) * mm, "end": v(57.94, 1.04) * mm});
            skLineSegment(sketch, "E970", {"start": v(57.94, 1.04) * mm, "end": v(57.94, 0.85) * mm});
            skLineSegment(sketch, "E971", {"start": v(57.94, 0.85) * mm, "end": v(57.94, 0.34) * mm});
            skLineSegment(sketch, "E972", {"start": v(57.94, 0.34) * mm, "end": v(57.94, -0.37) * mm});
            skLineSegment(sketch, "E973", {"start": v(57.94, -0.37) * mm, "end": v(57.94, -1.19) * mm});
            skLineSegment(sketch, "E974", {"start": v(57.94, -1.19) * mm, "end": v(57.94, -2) * mm});
            skLineSegment(sketch, "E975", {"start": v(57.94, -2) * mm, "end": v(57.94, -2.71) * mm});
            skLineSegment(sketch, "E976", {"start": v(57.94, -2.71) * mm, "end": v(57.94, -3.22) * mm});
            skLineSegment(sketch, "E977", {"start": v(57.94, -3.22) * mm, "end": v(57.94, -3.4) * mm});
            skLineSegment(sketch, "E978", {"start": v(57.94, -3.4) * mm, "end": v(57.84, -3.4) * mm});
            skLineSegment(sketch, "E979", {"start": v(57.84, -3.4) * mm, "end": v(57.73, -3.4) * mm});
            skLineSegment(sketch, "E980", {"start": v(57.73, -3.4) * mm, "end": v(57.73, -3.26) * mm});
            skLineSegment(sketch, "E981", {"start": v(57.73, -3.26) * mm, "end": v(57.73, -3.05) * mm});
            skLineSegment(sketch, "E982", {"start": v(57.73, -3.05) * mm, "end": v(57.55, -2.41) * mm});
            skLineSegment(sketch, "E983", {"start": v(57.55, -2.41) * mm, "end": v(57.12, -1.9) * mm});
            skLineSegment(sketch, "E984", {"start": v(57.12, -1.9) * mm, "end": v(57, -1.84) * mm});
            skLineSegment(sketch, "E985", {"start": v(57, -1.84) * mm, "end": v(56.94, -1.8) * mm});
            skLineSegment(sketch, "E986", {"start": v(56.94, -1.8) * mm, "end": v(56.35, -1.6) * mm});
            skLineSegment(sketch, "E987", {"start": v(56.35, -1.6) * mm, "end": v(56.16, -1.6) * mm});
            skLineSegment(sketch, "E988", {"start": v(56.16, -1.6) * mm, "end": v(55.78, -1.6) * mm});
            skLineSegment(sketch, "E989", {"start": v(55.78, -1.6) * mm, "end": v(54.95, -1.6) * mm});
            skLineSegment(sketch, "E990", {"start": v(54.95, -1.6) * mm, "end": v(54.12, -1.6) * mm});
            skLineSegment(sketch, "E991", {"start": v(54.12, -1.6) * mm, "end": v(53.75, -1.6) * mm});
            skLineSegment(sketch, "E992", {"start": v(53.75, -1.6) * mm, "end": v(53.75, -2.38) * mm});
            skLineSegment(sketch, "E993", {"start": v(53.75, -2.38) * mm, "end": v(53.75, -4.1) * mm});
            skLineSegment(sketch, "E994", {"start": v(53.75, -4.1) * mm, "end": v(53.75, -5.8) * mm});
            skLineSegment(sketch, "E995", {"start": v(53.75, -5.8) * mm, "end": v(53.75, -6.58) * mm});
            skLineSegment(sketch, "E996", {"start": v(53.75, -6.58) * mm, "end": v(54.14, -6.58) * mm});
            skLineSegment(sketch, "E997", {"start": v(54.14, -6.58) * mm, "end": v(55, -6.58) * mm});
            skLineSegment(sketch, "E998", {"start": v(55, -6.58) * mm, "end": v(55.87, -6.58) * mm});
            skLineSegment(sketch, "E999", {"start": v(55.87, -6.58) * mm, "end": v(56.26, -6.58) * mm});
            skLineSegment(sketch, "E1000", {"start": v(56.26, -6.58) * mm, "end": v(56.48, -6.57) * mm});
            skLineSegment(sketch, "E1001", {"start": v(56.48, -6.57) * mm, "end": v(57.47, -6.36) * mm});
            skLineSegment(sketch, "E1002", {"start": v(57.47, -6.36) * mm, "end": v(58.33, -5.9) * mm});
            skLineSegment(sketch, "E1003", {"start": v(58.33, -5.9) * mm, "end": v(58.48, -5.77) * mm});
            skLineSegment(sketch, "E1004", {"start": v(58.48, -5.77) * mm, "end": v(58.63, -5.64) * mm});
            skLineSegment(sketch, "E1005", {"start": v(58.63, -5.64) * mm, "end": v(59.27, -4.82) * mm});
            skLineSegment(sketch, "E1006", {"start": v(59.27, -4.82) * mm, "end": v(59.74, -3.8) * mm});
            skLineSegment(sketch, "E1007", {"start": v(59.74, -3.8) * mm, "end": v(59.81, -3.56) * mm});
            skLineSegment(sketch, "E1008", {"start": v(59.81, -3.56) * mm, "end": v(60, -3.56) * mm});
            skLineSegment(sketch, "E1009", {"start": v(60, -3.56) * mm, "end": v(59.96, -3.72) * mm});
            skLineSegment(sketch, "E1010", {"start": v(59.96, -3.72) * mm, "end": v(59.87, -4.16) * mm});
            skLineSegment(sketch, "E1011", {"start": v(59.87, -4.16) * mm, "end": v(59.75, -4.78) * mm});
            skLineSegment(sketch, "E1012", {"start": v(59.75, -4.78) * mm, "end": v(59.6, -5.49) * mm});
            skLineSegment(sketch, "E1013", {"start": v(59.6, -5.49) * mm, "end": v(59.46, -6.2) * mm});
            skLineSegment(sketch, "E1014", {"start": v(59.46, -6.2) * mm, "end": v(59.33, -6.81) * mm});
            skLineSegment(sketch, "E1015", {"start": v(59.33, -6.81) * mm, "end": v(59.24, -7.25) * mm});
            skLineSegment(sketch, "E1016", {"start": v(59.24, -7.25) * mm, "end": v(59.2, -7.42) * mm});
            skLineSegment(sketch, "E1017.bottom", {"start": v(-72.48, 12) * mm, "end": v(62.08, 12) * mm});
            skLineSegment(sketch, "E1017.top", {"start": v(-72.48, -12) * mm, "end": v(62.08, -12) * mm});
            skLineSegment(sketch, "E1017.left", {"start": v(-72.48, 12) * mm, "end": v(-72.48, -12) * mm});
            skLineSegment(sketch, "E1017.right", {"start": v(62.08, 12) * mm, "end": v(62.08, -12) * mm});
            skArc(sketch, "E1018", {"start": v(-72.48, 12) * mm, "mid": v(-84.48, 0) * mm, "end": v(-72.48, -12) * mm});
            skArc(sketch, "E1019", {"start": v(62.08, -12) * mm, "mid": v(74.08, 0) * mm, "end": v(62.08, 12) * mm});
            skCircle(sketch, "E1020", {"center": v(-72.48, 0) * mm, "radius": 9 * mm});
            skSolve(sketch);
        }
        {
            var Q0;
            Q0 = qSketchRegion(id + "F0", true);
            var Q1;
            Q1=makeQuery(id+"F0.imprint","IMPRINT",FACE,{"disambiguationData":[TD([[makeQuery(id+"F0.imprint","IMPRINT",EDGE,{"derivedFrom":sQuery(id+"F0.wireOp",EDGE,"E718")}),-1.0]])]});
            var Q2;
            Q2=makeQuery(id+"F0.imprint","IMPRINT",FACE,{"disambiguationData":[TD([[makeQuery(id+"F0.imprint","IMPRINT",EDGE,{"derivedFrom":sQuery(id+"F0.wireOp",EDGE,"E237")}),-1.0]])]});
            var Q3;
            {var subQ0=sQuery(id+"F0.wireOp",EDGE,"E1018");Q3=makeQuery(id+"F0.imprint","IMPRINT",FACE,{"disambiguationData":[TD([[makeQuery(id+"F0.imprint","IMPRINT",EDGE,{"derivedFrom":subQ0}),1.0]])]});}
            var Q4;
            {var subQ1=sQuery(id+"F0.wireOp",EDGE,"E1");Q4=makeQuery(id+"F0.imprint","IMPRINT",FACE,{"disambiguationData":[TD([[makeQuery(id+"F0.imprint","IMPRINT",EDGE,{"derivedFrom":subQ1}),1.0]])]});}
            var Q5;
            Q5=makeQuery(id+"F0.imprint","IMPRINT",FACE,{"disambiguationData":[TD([[makeQuery(id+"F0.imprint","IMPRINT",EDGE,{"derivedFrom":sQuery(id+"F0.wireOp",EDGE,"E3")}),-1.0]])]});
            var Q6;
            Q6=makeQuery(id+"F0.imprint","IMPRINT",FACE,{"disambiguationData":[TD([[makeQuery(id+"F0.imprint","IMPRINT",EDGE,{"derivedFrom":sQuery(id+"F0.wireOp",EDGE,"E440")}),1.0]])]});
            var Q7;
            Q7=makeQuery(id+"F0.imprint","IMPRINT",FACE,{"disambiguationData":[TD([[makeQuery(id+"F0.imprint","IMPRINT",EDGE,{"derivedFrom":sQuery(id+"F0.wireOp",EDGE,"E798")}),-1.0]])]});
            var Q8;
            {var subQ6=sQuery(id+"F0.wireOp",EDGE,"E3");Q8=makeQuery(id+"F0.imprint","IMPRINT",FACE,{"disambiguationData":[TD([[makeQuery(id+"F0.imprint","IMPRINT",EDGE,{"derivedFrom":subQ6}),1.0]])]});}
            var Q9;
            Q9=makeQuery(id+"F0.imprint","IMPRINT",FACE,{"disambiguationData":[TD([[makeQuery(id+"F0.imprint","IMPRINT",EDGE,{"derivedFrom":sQuery(id+"F0.wireOp",EDGE,"E347")}),-1.0]])]});
            var Q10;
            Q10=makeQuery(id+"F0.imprint","IMPRINT",FACE,{"disambiguationData":[TD([[makeQuery(id+"F0.imprint","IMPRINT",EDGE,{"derivedFrom":sQuery(id+"F0.wireOp",EDGE,"E103")}),1.0]])]});
            var Q11;
            Q11=makeQuery(id+"F0.imprint","IMPRINT",FACE,{"disambiguationData":[TD([[makeQuery(id+"F0.imprint","IMPRINT",EDGE,{"derivedFrom":sQuery(id+"F0.wireOp",EDGE,"E1017.right")}),1.0]])]});
            var Q12;
            Q12=makeQuery(id+"F0.imprint","IMPRINT",FACE,{"disambiguationData":[TD([[makeQuery(id+"F0.imprint","IMPRINT",EDGE,{"derivedFrom":sQuery(id+"F0.wireOp",EDGE,"E464")}),-1.0]])]});
            var Q13;
            Q13=makeQuery(id+"F0.imprint","IMPRINT",FACE,{"disambiguationData":[TD([[makeQuery(id+"F0.imprint","IMPRINT",EDGE,{"derivedFrom":sQuery(id+"F0.wireOp",EDGE,"E878")}),-1.0]])]});
            var Q14;
            Q14=makeQuery(id+"F0.imprint","IMPRINT",FACE,{"disambiguationData":[TD([[makeQuery(id+"F0.imprint","IMPRINT",EDGE,{"derivedFrom":sQuery(id+"F0.wireOp",EDGE,"E531")}),1.0]])]});
            var Q15;
            Q15=makeQuery(id+"F0.imprint","IMPRINT",FACE,{"disambiguationData":[TD([[makeQuery(id+"F0.imprint","IMPRINT",EDGE,{"derivedFrom":sQuery(id+"F0.wireOp",EDGE,"E579")}),-1.0]])]});
            var Q16;
            {var subQ4=sQuery(id+"F0.wireOp",EDGE,"E1");Q16=makeQuery(id+"F0.imprint","IMPRINT",FACE,{"disambiguationData":[TD([[makeQuery(id+"F0.imprint","IMPRINT",EDGE,{"derivedFrom":subQ4}),-1.0]])]});}
            extrude(context, id + "F1", {"entities" : qUnion([Q0, Q1, Q2, Q3, Q4, Q5, Q6, Q7, Q8, Q9, Q10, Q11, Q12, Q13, Q14, Q15, Q16]), "oppositeDirection" : true, "depth" : 6 * mm});
        }
        {
            var Q0;
            Q0=makeQuery(id+"F0.imprint","IMPRINT",FACE,{"disambiguationData":[TD([[makeQuery(id+"F0.imprint","IMPRINT",EDGE,{"derivedFrom":sQuery(id+"F0.wireOp",EDGE,"E3")}),-1.0]])]});
            var Q1;
            {var subQ1=sQuery(id+"F0.wireOp",EDGE,"E1");Q1=makeQuery(id+"F0.imprint","IMPRINT",FACE,{"disambiguationData":[TD([[makeQuery(id+"F0.imprint","IMPRINT",EDGE,{"derivedFrom":subQ1}),1.0]])]});}
            var Q2;
            Q2=makeQuery(id+"F0.imprint","IMPRINT",FACE,{"disambiguationData":[TD([[makeQuery(id+"F0.imprint","IMPRINT",EDGE,{"derivedFrom":sQuery(id+"F0.wireOp",EDGE,"E237")}),-1.0]])]});
            var Q3;
            Q3=makeQuery(id+"F0.imprint","IMPRINT",FACE,{"disambiguationData":[TD([[makeQuery(id+"F0.imprint","IMPRINT",EDGE,{"derivedFrom":sQuery(id+"F0.wireOp",EDGE,"E347")}),-1.0]])]});
            var Q4;
            Q4=makeQuery(id+"F0.imprint","IMPRINT",FACE,{"disambiguationData":[TD([[makeQuery(id+"F0.imprint","IMPRINT",EDGE,{"derivedFrom":sQuery(id+"F0.wireOp",EDGE,"E464")}),-1.0]])]});
            var Q5;
            Q5=makeQuery(id+"F0.imprint","IMPRINT",FACE,{"disambiguationData":[TD([[makeQuery(id+"F0.imprint","IMPRINT",EDGE,{"derivedFrom":sQuery(id+"F0.wireOp",EDGE,"E579")}),-1.0]])]});
            var Q6;
            Q6=makeQuery(id+"F0.imprint","IMPRINT",FACE,{"disambiguationData":[TD([[makeQuery(id+"F0.imprint","IMPRINT",EDGE,{"derivedFrom":sQuery(id+"F0.wireOp",EDGE,"E718")}),-1.0]])]});
            var Q7;
            Q7=makeQuery(id+"F0.imprint","IMPRINT",FACE,{"disambiguationData":[TD([[makeQuery(id+"F0.imprint","IMPRINT",EDGE,{"derivedFrom":sQuery(id+"F0.wireOp",EDGE,"E798")}),-1.0]])]});
            var Q8;
            Q8=makeQuery(id+"F0.imprint","IMPRINT",FACE,{"disambiguationData":[TD([[makeQuery(id+"F0.imprint","IMPRINT",EDGE,{"derivedFrom":sQuery(id+"F0.wireOp",EDGE,"E878")}),-1.0]])]});
            extrude(context, id + "F2", {"entities" : qUnion([Q0, Q1, Q2, Q3, Q4, Q5, Q6, Q7, Q8]), "operationType" : NewBodyOperationType.REMOVE, "oppositeDirection" : true, "depth" : 3 * mm});
        }
        {
            var Q0;
            Q0=makeQuery(id+"F1.opExtrude","CAP_EDGE",EDGE,{"disambiguationData":[OSD([sQuery(id+"F0.wireOp",EDGE,"E1018")])],"isStart":true});
            var Q1;
            Q1=makeQuery(id+"F1.opExtrude","CAP_EDGE",EDGE,{"disambiguationData":[OSD([sQuery(id+"F0.wireOp",EDGE,"E1017.top")])],"isStart":false});
            var Q2;
            Q2=makeQuery(id+"F1.opExtrude","CAP_EDGE",EDGE,{"disambiguationData":[OSD([sQuery(id+"F0.wireOp",EDGE,"E1020")])],"isStart":true});
            var Q3;
            Q3=makeQuery(id+"F1.opExtrude","CAP_EDGE",EDGE,{"disambiguationData":[OSD([sQuery(id+"F0.wireOp",EDGE,"E1020")])],"isStart":false});
            fillet(context, id + "F3", {"entities" : qUnion([Q0, Q1, Q2, Q3]), "radius" : 1.5 * mm, "tangentPropagation" : true, "allowEdgeOverflow" : false});
        }
    });
